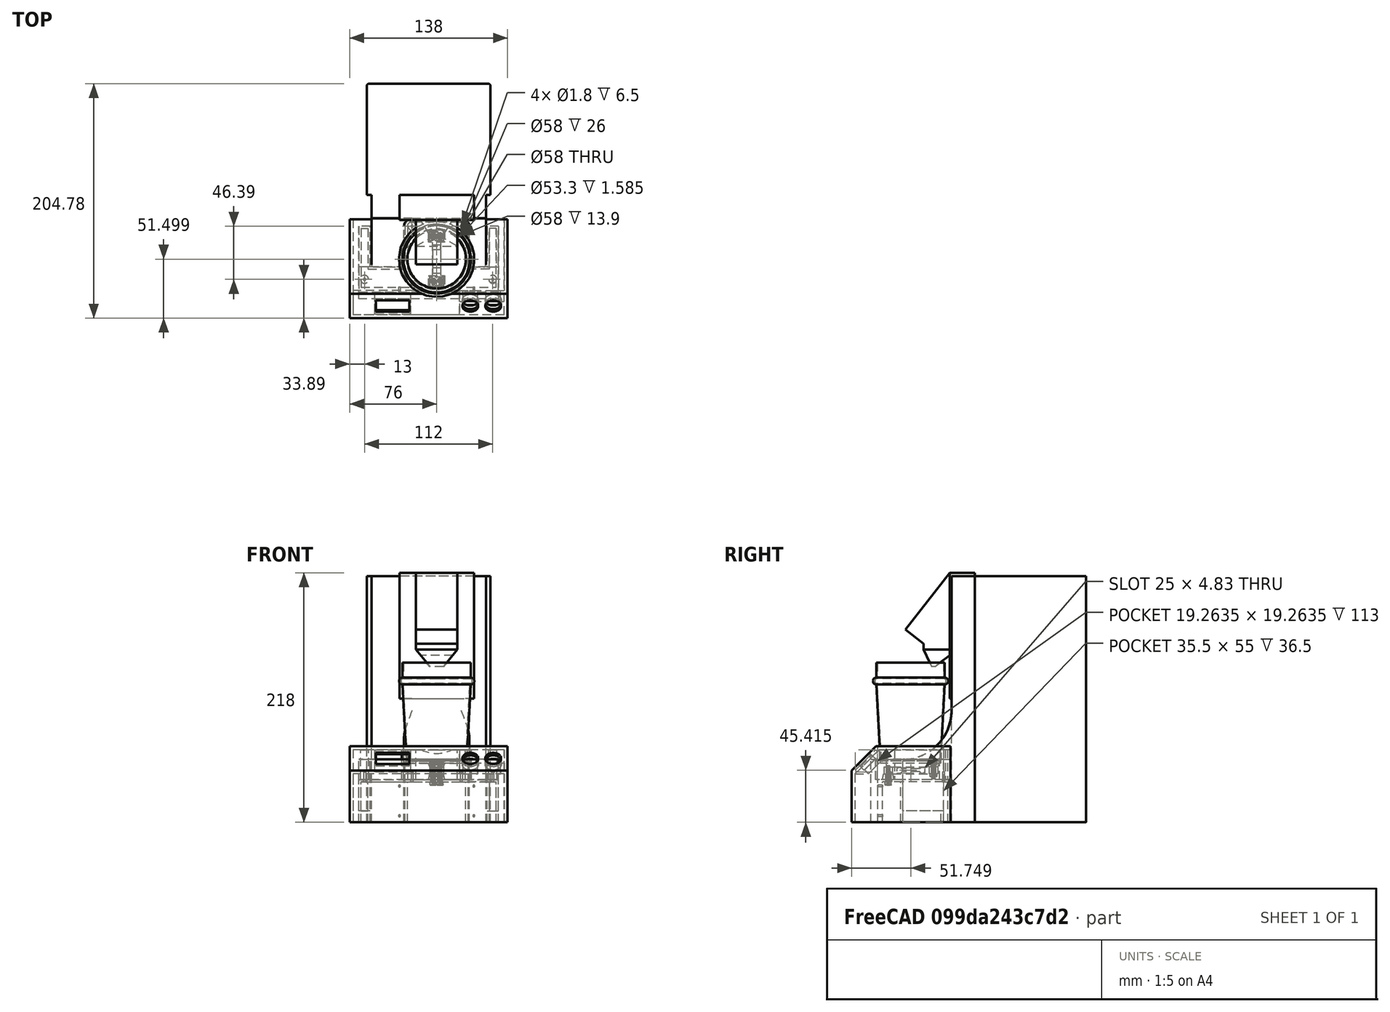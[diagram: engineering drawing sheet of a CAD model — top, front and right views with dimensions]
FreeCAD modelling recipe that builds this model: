
FCSTD DOCUMENT  (FreeCAD 0.20R29410 (Git))
Label: muehle-waage
License: All rights reserved
LicenseURL: http://en.wikipedia.org/wiki/All_rights_reserved
objects: Sketcher::SketchObject×45, PartDesign::Plane×34, PartDesign::Pad×21, PartDesign::Pocket×18, PartDesign::ShapeBinder×14, PartDesign::Body×10, Mesh::Feature×9, Part::FeaturePython×6, Part::Cut×3, PartDesign::AdditiveLoft×2, Spreadsheet::Sheet×1, PartDesign::Revolution×1, PartDesign::Fillet×1
note: 198 computed .brp shape members not serialized (recipe doc carries the construction recipe); baked Part::Feature solids carry a one-line shape summary decoded from their .brp

FEATURE [Spreadsheet::Sheet] Spreadsheet  label="s"
  cells = A1=Sketch fuer Muehle Base; C1=Sketch fuer Adapter; E1=Sketch fuer Dose; G1=Base Plate Waage; I1=Waegezelle; K1=Clips; M1=Cover; O1=Display; Q1=Buttons; A2=(alles in mm); K2=sind zu Threaded Inserts geworden; A3=radius_fuss_aussenseite; B3(radius_fuss_aussenseite)=2; C3=spalt_zur_muehle; D3(spalt_zur_muehle)=1; E3=dose_durchmesser; F3(dose_durchmesser)=58; G3=z_m3_schraube_gewinde; H3(z_m3_schraube_gewinde)=16; I3=y_wz_abstand_loecher; J3(y_wz_abstand_loecher)=40; K3=durchmesser_clips_loch; L3(durchmesser_clips_loch)=2; M3=z_hoehe_ueber_base_plate; N3(z_hoehe_ueber_base_plate)=10; O3=display_breite; P3(display_breite)=29; Q3=button_abstand; R3(button_abstand)=10; A4=radius_fuss_innenseite; B4(radius_fuss_innenseite)=7; C4=x_seitlich_von_muehle; D4(x_seitlich_von_muehle)=10; E4=dose_wandstaerke; F4(dose_wandstaerke)=0.9; G4=z_m3_schraube_kopf; H4(z_m3_schraube_kopf)=3.2; I4=y_wz_gesamt; J4(y_wz_gesamt)=47; K4=durchmesser; L4(durchmesser_loch_threaded_inserts)=1.8; M4=y_abstand_cover_zu_vorderseite_teil; N4(y_abstand_cover_zu_vorderseite_teil)=20; O4=display_hoehe; P4(display_hoehe)=14; Q4=button_kappe_durchmesser; R4(button_kappe_durchmesser)=13.8; A5=radius_rueckseite; B5(radius_rueckseite)=2; C5=y_hauptteil; D5(y_hauptteil)=28; E5=dose_durchmesser_ring; F5(dose_durchmesser_ring)=6; G5=z_pad_hoehe_base_plate; H5(z_pad_hoehe_base_plate)=2; I5=y_wz_kurz; J5(y_wz_kurz)=7.5; K5=pocket_depth_threaded_inserts; L5(pocket_depth_threaded_inserts)=6.5; M5=dicke_cover; N5(dicke_cover)=3; O5=display_pcb_breite; P5(display_pcb_breite)=31; Q5=button_kappe_hoehe; R5(button_kappe_hoehe)=4; E6=dose_durchmesser_unten; F6(dose_durchmesser_unten)=52.8; G6=durchmesser_m3_schraube_kopf; H6(durchmesser_m3_schraube_kopf)=5.5; I6=x_wz_min; J6(x_wz_min)=7; M6=laenge_schraege_seite; N6(laenge_schraege_seite)=30; O6=display_pcb_hoehe; P6(display_pcb_hoehe)=25; Q6=button_kappe_ueberstand; R6(button_kappe_ueberstand)=1; C7=adapter_pad_hoehe; D7(adapter_pad_hoehe)=55; G7=z_standoff_hoehe; H7(z_standoff_hoehe)=3; I7=x_wz_max; J7(x_wz_max)=12; M7=x_ueberstand_cover; N7(x_ueberstand_cover)=5; O7=display_extrusion; P7(display_extrusion)=2; Q7=button_kappe_durchmesser_gross; R7(button_kappe_durchmesser_gross)=14; E8=y_abstand_dose; F8(y_abstand_dose)=-12; G8=y_standoff_gross; H8(y_standoff_gross)=10; I8=x_wz_abstand_loecher; J8(x_wz_abstand_loecher)=6; M8=x_pad_cover; N8(x_pad_cover)==breite_gesamt_unten + 2 * spalt_zur_muehle + 2 * x_seitlich_von_muehle + 2 * x_ueberstand_cover; O8=display_pcb_extrusion; P8(display_pcb_extrusion)=5; Q8=button_kappe_gross_hoehe; R8(button_kappe_gross_hoehe)=4.5; A9=hoehe_gesamt; B9(hoehe_gesamt)=160; C9=spalt_zur_dose; D9(spalt_zur_dose)=0.5; G9=y_standoff_klein; H9(y_standoff_klein)=8; I9=durchmesser_wz_loecher_klein; J9(durchmesser_wz_loecher_klein)=3; M9=dose_verstaerkung_breite; N9(dose_verstaerkung_breite)=1.5; P9=actually 1, but made larger for booleon subtraction from cover; Q9=button_base_seitenlaenge; R9(button_base_seitenlaenge)=13; A10=hoehe_blech; B10(hoehe_blech)=97; E10=z_dose_hoehe; F10(z_dose_hoehe)=86; G10=x_standoff_gross; H10(x_standoff_gross)=14; I10=durchmesser_wz_loecher_gross; J10(durchmesser_wz_loecher_gross)=3.5; M10=dose_verstaerkung_pad; N10(dose_verstaerkung_pad)=5; O10=display_abstand_von_links; P10(display_abstand_von_links)=20; Q10=button_base_extrusion; R10(button_base_extrusion)=15; A11=hoehe_fuss; B11(hoehe_fuss)=42.5; E11=z_abstand_dose_von_schnauze; F11(z_abstand_dose_von_schnauze)=16; G11=x_standoff_klein; H11(x_standoff_klein)=12; I11=z_wz_pad; J11(z_wz_pad)=6; M11=durchmesser_pillars; N11(durchmesser_pillars)=7; O11=ende_display_von_links; P11(ende_display_von_links)==display_abstand_von_links + display_breite; R11=actually 3,5, but cranked up to fit; A12=breite_gesamt_oben; B12(breite_gesamt_oben)=108; C12="Teil" an der WZ; E12=z_dose_oberhalb_ring; F12(z_dose_oberhalb_ring)=13; G12=spalt_pocket_schraubenkopf; H12(spalt_pocket_schraubenkopf)=0.3; I12=durchmesser_wz_bohrung; J12(durchmesser_wz_bohrung)=5; Q12=button1_abstand_von_links; A13=breite_gesamt_unten; B13(breite_gesamt_unten)=100; C13=z_standoff_hoehe_am_teil; D13(z_standoff_hoehe_am_teil)=5; I13=y_laenge_wz_slot; J13(y_laenge_wz_slot)=25; A14=breite_zwischen_fuessen; B14(breite_zwischen_fuessen)=58; C14=y_abstand_standoff_vorderseite; D14(y_abstand_standoff_vorderseite)=4; E14=dose_fillet_radius; F14(dose_fillet_radius)=2; I14=z_hoehe_wz_slot; J14(z_hoehe_wz_slot)=2.5; A15=breite_linker_fuss; B15(breite_linker_fuss)=28.5; C15=wandstaerke_pocket_mitte; D15(wandstaerke_pocket_mitte)=2; A16=breite_rechter_fuss; B16(breite_rechter_fuss)=14.5; C17=m3_bohrung (WZ); D17(m3_bohrung)=4; A18=extrusion_hoehe_muehle; B18(extrusion_hoehe_muehle)=215; C18=m2_bohrung (MoBo); D18(m2_bohrung)=1.8; A19=extrusion_hoehe_fuesse; B19(extrusion_hoehe_fuesse)=55; C19=x_abstand_threaded_inserts; D19(x_abstand_threaded_inserts)=65; C20=z_abstand_threaded_inserts; D20(z_abstand_threaded_inserts)==32 - 3 - 3; A21=x_muehle_verzierung; B21(x_muehle_verzierung)=65; C21=x_abstand_threaded_inserts_von_seite; D21(x_abstand_threaded_inserts_von_seite)=17; A22=y_extrusion_muehle_verzierung; B22(y_extrusion_muehle_verzierung)==hoehe_gesamt - hoehe_blech - hoehe_fuss + y_offset_muehle_verzierung; C22=m3_mutter_breite; D22(m3_mutter_breite)=4; E22=!! actually M2 :/; A23=z_verzierung; B23(z_verzierung)=110; C23=m3_mutter_hoehe; D23(m3_mutter_hoehe)=1.6; E23=!! actually M2 :/; A24=y_offset_muehle_verzierung; B24(y_offset_muehle_verzierung)=1.5; A25=z_offset_muehle_verzierung; +28 more cells
FEATURE [Sketcher::SketchObject] Sketch  label="muehle_base"
  FullyConstrained = true
  MapMode = 5
  Support = -> [XY_Plane]
  expr: Constraints[47] = <<s>>.radius_fuss_aussenseite
  expr: Constraints[48] = <<s>>.radius_fuss_aussenseite
  expr: Constraints[50] = <<s>>.radius_fuss_innenseite
  expr: Constraints[53] = Spreadsheet.breite_gesamt_oben
  expr: Constraints[54] = <<s>>.breite_gesamt_unten
  expr: Constraints[55] = <<s>>.hoehe_gesamt
  expr: Constraints[57] = <<s>>.radius_rueckseite
  expr: Constraints[58] = <<s>>.hoehe_blech
  expr: Constraints[59] = <<s>>.breite_linker_fuss
  expr: Constraints[60] = <<s>>.hoehe_fuss
  expr: Constraints[61] = <<s>>.breite_rechter_fuss
  sketch-geometry (20):
    g0: LineSegment StartX=-54 StartY=95 StartZ=0 EndX=-54 EndY=0 EndZ=0
    g1: LineSegment StartX=-54 StartY=0 StartZ=0 EndX=-50 EndY=0 EndZ=0
    g2: LineSegment StartX=-50 StartY=0 StartZ=0 EndX=-50 EndY=-61 EndZ=0
    g3: ArcOfCircle CenterX=-48 CenterY=-61 CenterZ=0 NormalX=0 NormalY=0 NormalZ=1 AngleXU=0 Radius=2 StartAngle=3.14159 EndAngle=4.71239
    g4: LineSegment StartX=-48 StartY=-63 StartZ=0 EndX=-23.5 EndY=-63 EndZ=0
    g5: ArcOfCircle CenterX=-23.5 CenterY=-61 CenterZ=0 NormalX=0 NormalY=0 NormalZ=1 AngleXU=0 Radius=2 StartAngle=4.71239 EndAngle=6.28319
    g6: LineSegment StartX=-21.5 StartY=-61 StartZ=0 EndX=-21.5 EndY=-27.5 EndZ=0
    g7: ArcOfCircle CenterX=-14.5 CenterY=-27.5 CenterZ=0 NormalX=0 NormalY=0 NormalZ=1 AngleXU=0 Radius=7 StartAngle=1.5708 EndAngle=3.14159
    g8: LineSegment StartX=-14.5 StartY=-20.5 StartZ=0 EndX=28.5 EndY=-20.5 EndZ=0
    g9: ArcOfCircle CenterX=28.5 CenterY=-27.5 CenterZ=0 NormalX=0 NormalY=0 NormalZ=1 AngleXU=0 Radius=7 StartAngle=0 EndAngle=1.5708
    g10: LineSegment StartX=35.5 StartY=-27.5 StartZ=0 EndX=35.5 EndY=-61 EndZ=0
    g11: ArcOfCircle CenterX=37.5 CenterY=-61 CenterZ=0 NormalX=0 NormalY=0 NormalZ=1 AngleXU=0 Radius=2 StartAngle=3.14159 EndAngle=4.71239
    g12: LineSegment StartX=37.5 StartY=-63 StartZ=0 EndX=48 EndY=-63 EndZ=0
    g13: ArcOfCircle CenterX=48 CenterY=-61 CenterZ=0 NormalX=0 NormalY=0 NormalZ=1 AngleXU=0 Radius=2 StartAngle=4.71239 EndAngle=6.28319
    g14: LineSegment StartX=50 StartY=-61 StartZ=0 EndX=50 EndY=0 EndZ=0
    g15: LineSegment StartX=50 StartY=0 StartZ=0 EndX=54 EndY=0 EndZ=0
    g16: LineSegment StartX=54 StartY=0 StartZ=0 EndX=54 EndY=95 EndZ=0
    g17: ArcOfCircle CenterX=52 CenterY=95 CenterZ=0 NormalX=0 NormalY=0 NormalZ=1 AngleXU=0 Radius=2 StartAngle=1.9e-15 EndAngle=1.5708
    g18: LineSegment StartX=52 StartY=97 StartZ=0 EndX=-52 EndY=97 EndZ=0
    g19: ArcOfCircle CenterX=-52 CenterY=95 CenterZ=0 NormalX=0 NormalY=0 NormalZ=1 AngleXU=0 Radius=2 StartAngle=1.5708 EndAngle=3.14159
  constraints (62):
    c: Vertical(g0)
    c: Horizontal(g1)
    c: Coincident(g1,g2)
    c: Tangent(g2,g3) = -1.5708
    c: Coincident(g3,g4)
    c: Horizontal(g4)
    c: Tangent(g4,g5) = -1.5708
    c: Coincident(g5,g6)
    c: Vertical(g6)
    c: Tangent(g6,g7) = 1.5708
    c: Coincident(g7,g8)
    c: Horizontal(g8)
    c: Tangent(g8,g9) = 1.5708
    c: Coincident(g9,g10)
    c: Vertical(g10)
    c: Tangent(g10,g11) = -1.5708
    c: Coincident(g11,g12)
    c: Horizontal(g12)
    c: Coincident(g13,g14)
    c: Vertical(g14)
    c: Coincident(g14,g15)
    c: Coincident(g15,g16)
    c: Vertical(g16)
    c: Tangent(g16,g17) = -1.5708
    c: Coincident(g17,g18)
    c: Horizontal(g18)
    c: Coincident(g19,g0)
    c: Horizontal(g0,g16)
    c: Coincident(g1,g0)
    c: Horizontal(g15)
    c: Horizontal(g2,g5)
    c: Horizontal(g10,g13)
    c: Horizontal(g6,g9)
    c: Coincident(g19,g18)
    c: Vertical(g18,g19)
    c: Symmetric(g0,g15,g-1)
    c: Vertical(g11,g11)
    c: Coincident(g12,g13)
    c: Horizontal(g13,g13)
    c: Vertical(g13,g12)
    c: Horizontal(g9,g9)
    c: Vertical(g7,g7)
    c: Horizontal(g2,g3)
    c: Horizontal(g3,g3)
    c: Horizontal(g3,g5)
    c: Horizontal(g5,g5)
    c: Vertical(g3,g3)
    c: Radius(g3) = 2
    c: Radius(g11) = 2
    c: Horizontal(g10,g5)
    c: Radius(g7) = 7
    c: Vertical(g17,g17)
    c: Symmetric(g1,g14,g-2)
    c: DistanceX(g0,g16) = 108
    c: DistanceX(g2,g13) = 100
    c: DistanceY(g3,g18) = 160
    c: Horizontal(g19,g0)
    c: Radius(g19) = 2
    c: DistanceY(g0,g18) = 97
    c: DistanceX(g2,g5) = 28.5
    c: DistanceY(g4,g7) = 42.5
    c: DistanceX(g10,g13) = 14.5
FEATURE [PartDesign::Pad] Pad
  Direction = (0,0,1)
  Length = 215
  Length2 = 10
  Profile = -> Sketch
  ReferenceAxis = -> Sketch [N_Axis]
  Type = 0
  expr: Length = <<s>>.extrusion_hoehe_muehle
FEATURE [PartDesign::Plane] DatumPlane  label="DatumPlanePocketFuss"
  Length = 199.436
  MapMode = 5
  Placement = pos=(50,0,0) rot=(0.57735,0.57735,0.57735;2.0944rad)
  ResizeMode = 0
  Support = -> [Pad]
  Width = 282.436
FEATURE [Sketcher::SketchObject] Sketch001
  ExternalGeometry = -> [Pad]
  FullyConstrained = true
  MapMode = 5
  Placement = pos=(50,0,0) rot=(0.57735,0.57735,0.57735;2.0944rad)
  Support = -> [DatumPlane]
  expr: Constraints[10] = <<s>>.hoehe_fuss
  expr: Constraints[13] = <<s>>.extrusion_hoehe_fuesse
  sketch-geometry (5):
    g0: LineSegment StartX=-20.5 StartY=220 StartZ=0 EndX=-20.5 EndY=97.5 EndZ=0
    g1: ArcOfCircle CenterX=-63 CenterY=97.5 CenterZ=0 NormalX=0 NormalY=0 NormalZ=1 AngleXU=0 Radius=42.5 StartAngle=4.71239 EndAngle=6.28319
    g2: LineSegment StartX=-63 StartY=55 StartZ=0 EndX=-68 EndY=55 EndZ=0
    g3: LineSegment StartX=-68 StartY=55 StartZ=0 EndX=-68 EndY=220 EndZ=0
    g4: LineSegment StartX=-68 StartY=220 StartZ=0 EndX=-20.5 EndY=220 EndZ=0
  constraints (14):
    c: Vertical(g0)
    c: Tangent(g0,g1) = 1.5708
    c: Tangent(g1,g2) = 1.5708
    c: Coincident(g2,g3)
    c: Vertical(g3)
    c: Coincident(g3,g4)
    c: Coincident(g4,g0)
    c: Horizontal(g4)
    c: PointOnObject(g1,g-3)
    c: Vertical(g1,g1)
    c: Radius(g1) = 42.5
    c: DistanceY(g-3,g3) = 5
    c: DistanceX(g3,g-3) = 5
    c: DistanceY(g-3,g1) = 55
FEATURE [PartDesign::Pocket] Pocket
  BaseFeature = -> Pad
  Direction = (-1,0,0)
  Length = 5
  Length2 = 5
  Profile = -> Sketch001
  ReferenceAxis = -> Sketch001 [N_Axis]
  Type = 1
FEATURE [PartDesign::Plane] DatumPlane001  label="DatumPlaneVerzierungMuehle"
  Length = 140.4
  MapMode = 5
  Placement = pos=(0,0,0) rot=(1,0,0;1.5708rad)
  ResizeMode = 0
  Support = -> [Pocket]
  Width = 275.4
FEATURE [Mesh::Feature] Mesh  label="TestMesh001"
FEATURE [PartDesign::Plane] DatumPlane004  label="DatumPlaneMitteVonSchnauze"
  AttachmentOffset = pos=(0,0,7) rot=(0,0,1;0rad)
  Length = 199.436
  MapMode = 5
  Placement = pos=(7,-1.6e-15,1.6e-15) rot=(0.57735,0.57735,0.57735;2.0944rad)
  ResizeMode = 0
  Support = -> [YZ_Plane]
  Width = 282.436
  expr: .AttachmentOffset.Base.z = <<s>>.offset_yz
FEATURE [Sketcher::SketchObject] Sketch003  label="SketchVerzierung"
  ExternalGeometry = -> [Pocket,DatumPlane004]
  FullyConstrained = true
  MapMode = 5
  Placement = pos=(0,0,0) rot=(1,0,0;1.5708rad)
  Support = -> [DatumPlane001]
  expr: Constraints[7] = Spreadsheet.x_muehle_verzierung
  expr: Constraints[8] = Spreadsheet.z_verzierung
  expr: Constraints[9] = <<s>>.z_offset_muehle_verzierung
  sketch-geometry (4):
    g0: LineSegment StartX=-25.5 StartY=218 StartZ=0 EndX=-25.5 EndY=108 EndZ=0
    g1: LineSegment StartX=-25.5 StartY=108 StartZ=0 EndX=39.5 EndY=108 EndZ=0
    g2: LineSegment StartX=39.5 StartY=108 StartZ=0 EndX=39.5 EndY=218 EndZ=0
    g3: LineSegment StartX=39.5 StartY=218 StartZ=0 EndX=-25.5 EndY=218 EndZ=0
  constraints (11):
    c: Coincident(g0,g1)
    c: Coincident(g1,g2)
    c: Coincident(g2,g3)
    c: Coincident(g3,g0)
    c: Horizontal(g3)
    c: Vertical(g0)
    c: Vertical(g2)
    c: DistanceX(g3,g3) = 65
    c: DistanceY(g0,g0) = 110
    c: DistanceY(g-3,g0) = 3
    c: Symmetric(g0,g1,g-4)
FEATURE [PartDesign::Pad] Pad002  label="PadVerzierung"
  BaseFeature = -> Pocket
  Direction = (0,-1,2e-16)
  Length = 22
  Length2 = 10
  Profile = -> Sketch003
  ReferenceAxis = -> Sketch003 [N_Axis]
  Type = 0
  expr: Length = <<s>>.y_extrusion_muehle_verzierung
FEATURE [Sketcher::SketchObject] Sketch004  label="SketchSchnauze"
  ExternalGeometry = -> [Pad002]
  FullyConstrained = true
  MapMode = 2
  Placement = pos=(7,-1.6e-15,1.6e-15) rot=(0.57735,0.57735,0.57735;2.0944rad)
  Support = -> [DatumPlane004]
  expr: Constraints[7] = <<s>>.z_schnauze
  expr: Constraints[8] = <<s>>.y_schnauze
  expr: Constraints[9] = <<s>>.l_schnauze_schraege
  sketch-geometry (4):
    g0: LineSegment StartX=-22 StartY=218 StartZ=0 EndX=-60.7693 EndY=168.302 EndZ=0
    g1: LineSegment StartX=-60.7693 StartY=168.302 StartZ=0 EndX=-45 EndY=156 EndZ=0
    g2: LineSegment StartX=-45 StartY=156 StartZ=0 EndX=-22 EndY=156 EndZ=0
    g3: LineSegment StartX=-22 StartY=156 StartZ=0 EndX=-22 EndY=218 EndZ=0
  constraints (11):
    c: Coincident(g0,g1)
    c: Coincident(g1,g2)
    c: Horizontal(g2)
    c: Coincident(g2,g3)
    c: Coincident(g3,g0)
    c: Vertical(g3)
    c: Coincident(g0,g-3)
    c: DistanceY(g3,g3) = 62
    c: DistanceX(g2,g2) = 23
    c: Distance(g1) = 20
    c: Angle(g1,g0) = 1.5708
FEATURE [PartDesign::Pad] Pad003  label="PadSchnauze"
  BaseFeature = -> Pad002
  Direction = (1,-1e-16,1e-16)
  Length = 36
  Length2 = 10
  Midplane = true
  Profile = -> Sketch004
  ReferenceAxis = -> Sketch004 [N_Axis]
  Type = 0
  expr: Length = <<s>>.x_schnauze
FEATURE [PartDesign::Plane] DatumPlane002  label="DatumPlanePlastikPadUnterSchnauze"
  Length = 140.4
  MapMode = 5
  Placement = pos=(0,-22,4.9e-15) rot=(1,0,0;1.5708rad)
  ResizeMode = 0
  Support = -> [Pad003]
  Width = 275.4
FEATURE [Sketcher::SketchObject] Sketch005  label="SketchPlastikUnterSchnauze"
  ExternalGeometry = -> [Pad003,DatumPlane004]
  FullyConstrained = true
  MapMode = 5
  Placement = pos=(0,-22,4.9e-15) rot=(1,0,0;1.5708rad)
  Support = -> [DatumPlane002]
  expr: Constraints[0] = <<s>>.x_kurz_plastik_unter_schnauze
  expr: Constraints[1] = <<s>>.z_plastik_unter_schnauze
  expr: Constraints[9] = <<s>>.z_lippe_plastik_unter_schnauze
  sketch-geometry (6):
    g0: LineSegment StartX=13 StartY=136 StartZ=0 EndX=1 EndY=136 EndZ=0
    g1: LineSegment StartX=-11 StartY=156 StartZ=0 EndX=-11 EndY=151 EndZ=0
    g2: LineSegment StartX=-11 StartY=151 StartZ=0 EndX=1 EndY=136 EndZ=0
    g3: LineSegment StartX=25 StartY=156 StartZ=0 EndX=25 EndY=151 EndZ=0
    g4: LineSegment StartX=25 StartY=151 StartZ=0 EndX=13 EndY=136 EndZ=0
    g5: LineSegment StartX=-11 StartY=156 StartZ=0 EndX=25 EndY=156 EndZ=0
  constraints (15):
    c: DistanceX(g0,g0) = 12
    c: DistanceY(g0,g-3) = 20
    c: Vertical(g1)
    c: Coincident(g1,g2)
    c: Coincident(g2,g0)
    c: Coincident(g3,g4)
    c: Coincident(g4,g0)
    c: Vertical(g3)
    c: Horizontal(g3,g1)
    c: DistanceY(g1,g1) = 5
    c: Symmetric(g0,g0,g-4)
    c: Coincident(g1,g-3)
    c: Symmetric(g3,g1,g-4)
    c: Coincident(g5,g1)
    c: Coincident(g5,g3)
FEATURE [PartDesign::Pad] Pad004  label="PadMuehleKomplett"
  BaseFeature = -> Pad003
  Direction = (0,-1,2e-16)
  Length = 23
  Length2 = 10
  Profile = -> Sketch005
  ReferenceAxis = -> Sketch005 [N_Axis]
  Type = 0
  expr: Length = <<s>>.y_extrusion_plastik_unter_schnauze
FEATURE [PartDesign::Plane] DatumPlane003  label="DatumPlanePlastikUnterSchnauzePocket"
  Length = 199.436
  MapMode = 5
  Placement = pos=(25,0,0) rot=(0.57735,0.57735,0.57735;2.0944rad)
  ResizeMode = 0
  Support = -> [Pad004]
  Width = 282.436
FEATURE [Sketcher::SketchObject] Sketch007
  ExternalGeometry = -> [Pad004]
  FullyConstrained = true
  MapMode = 5
  Placement = pos=(25,0,0) rot=(0.57735,0.57735,0.57735;2.0944rad)
  Support = -> [DatumPlane003]
  expr: Constraints[14] = <<s>>.y_plastik_unter_schnauze_pocket_kurz
  expr: Constraints[17] = <<s>>.y_abstand_plastik_unter_schnauze_von_muehle_body_unten
  expr: Constraints[19] = <<s>>.z_plastik_unter_schnauze_pocket_hinten
  sketch-geometry (7):
    g0: LineSegment StartX=-45 StartY=151 StartZ=0 EndX=-38 EndY=136 EndZ=0
    g1: LineSegment StartX=-38 StartY=136 StartZ=0 EndX=-35 EndY=136 EndZ=0
    g2: LineSegment StartX=-35 StartY=136 StartZ=0 EndX=-22 EndY=146 EndZ=0
    g3: LineSegment StartX=-45 StartY=151 StartZ=0 EndX=-46 EndY=151 EndZ=0
    g4: LineSegment StartX=-46 StartY=151 StartZ=0 EndX=-46 EndY=135 EndZ=0
    g5: LineSegment StartX=-46 StartY=135 StartZ=0 EndX=-22 EndY=135 EndZ=0
    g6: LineSegment StartX=-22 StartY=135 StartZ=0 EndX=-22 EndY=146 EndZ=0
  constraints (20):
    c: Coincident(g-3,g0)
    c: Coincident(g0,g1)
    c: Horizontal(g1)
    c: Coincident(g1,g2)
    c: Coincident(g0,g3)
    c: Horizontal(g3)
    c: Coincident(g3,g4)
    c: Vertical(g4)
    c: Coincident(g4,g5)
    c: Horizontal(g5)
    c: Coincident(g5,g6)
    c: Coincident(g6,g2)
    c: Vertical(g6)
    c: Horizontal(g0,g-4)
    c: DistanceX(g1,g1) = 3
    c: DistanceX(g4,g-4) = 1
    c: DistanceY(g4,g-4) = 1
    c: DistanceX(g0,g-5) = 16
    c: Vertical(g-5,g2)
    c: DistanceY(g2,g-3) = 10
FEATURE [PartDesign::Pocket] Pocket001  label="PocketPlastikUnterSchnauze"
  AlongSketchNormal = false
  BaseFeature = -> Pad004
  Direction = (-1,0,0)
  Length = 5
  Length2 = 5
  Profile = -> Sketch007
  ReferenceAxis = -> Sketch007 [N_Axis]
  Type = 1
FEATURE [PartDesign::Body] Body  label="muehle"
  Group = -> [Sketch,Pad,DatumPlane,Sketch001,Pocket,DatumPlane004,DatumPlane001,Sketch003,Pad002,Sketch004,Pad003,DatumPlane002,Sketch005,Pad004,DatumPlane003,Sketch007,Pocket001]
  Origin = -> Origin
  Tip = -> Pocket001
FEATURE [PartDesign::ShapeBinder] ShapeBinder002  label="ShapeBinderMuehle001"
  Support = -> [Sketch]
  TraceSupport = false
FEATURE [Sketcher::SketchObject] Sketch002  label="sketch_adapter"
  ExternalGeometry = -> [ShapeBinder002]
  FullyConstrained = true
  MapMode = 5
  Support = -> [XY_Plane003]
  expr: Constraints[24] = Spreadsheet.x_seitlich_von_muehle
  expr: Constraints[25] = Spreadsheet.y_hauptteil
  expr: Constraints[38] = <<s>>.spalt_zur_muehle
  expr: Constraints[41] = <<s>>.spalt_zur_muehle
  expr: Constraints[42] = <<s>>.spalt_zur_muehle
  sketch-geometry (14):
    g0: LineSegment StartX=-61 StartY=-27.5 StartZ=0 EndX=-51 EndY=-27.5 EndZ=0
    g1: LineSegment StartX=-51 StartY=-27.5 StartZ=0 EndX=-51 EndY=-63 EndZ=0
    g2: LineSegment StartX=-51 StartY=-63 StartZ=0 EndX=-20.5 EndY=-63 EndZ=0
    g3: LineSegment StartX=-20.5 StartY=-63 StartZ=0 EndX=-20.5 EndY=-27.5 EndZ=0
    g4: LineSegment StartX=34.5 StartY=-27.5 StartZ=0 EndX=34.5 EndY=-63 EndZ=0
    g5: LineSegment StartX=34.5 StartY=-63 StartZ=0 EndX=51 EndY=-63 EndZ=0
    g6: LineSegment StartX=51 StartY=-63 StartZ=0 EndX=51 EndY=-27.5 EndZ=0
    g7: LineSegment StartX=51 StartY=-27.5 StartZ=0 EndX=61 EndY=-27.5 EndZ=0
    g8: LineSegment StartX=61 StartY=-27.5 StartZ=0 EndX=61 EndY=-91 EndZ=0
    g9: LineSegment StartX=61 StartY=-91 StartZ=0 EndX=-61 EndY=-91 EndZ=0
    g10: LineSegment StartX=-61 StartY=-91 StartZ=0 EndX=-61 EndY=-27.5 EndZ=0
    g11: LineSegment StartX=-14.5 StartY=-21.5 StartZ=0 EndX=28.5 EndY=-21.5 EndZ=0
    g12: ArcOfCircle CenterX=-14.5 CenterY=-27.5 CenterZ=0 NormalX=0 NormalY=0 NormalZ=1 AngleXU=0 Radius=6 StartAngle=1.5708 EndAngle=3.14159
    g13: ArcOfCircle CenterX=28.5 CenterY=-27.5 CenterZ=0 NormalX=0 NormalY=0 NormalZ=1 AngleXU=0 Radius=6 StartAngle=0 EndAngle=1.5708
  constraints (43):
    c: Horizontal(g0)
    c: Coincident(g0,g1)
    c: Vertical(g1)
    c: Coincident(g1,g2)
    c: Horizontal(g2)
    c: Coincident(g2,g3)
    c: Vertical(g3)
    c: Vertical(g4)
    c: Coincident(g4,g5)
    c: Horizontal(g5)
    c: Coincident(g5,g6)
    c: Vertical(g6)
    c: Coincident(g6,g7)
    c: Horizontal(g7)
    c: Coincident(g7,g8)
    c: Vertical(g8)
    c: Coincident(g8,g9)
    c: Horizontal(g9)
    c: Coincident(g9,g10)
    c: Coincident(g10,g0)
    c: Vertical(g10)
    c: Horizontal(g0,g3)
    c: Horizontal(g4,g6)
    c: Equal(g0,g7)
    c: DistanceX(g0,g0) = 10
    c: DistanceY(g9,g1) = 28
    c: Horizontal(g4,g2)
    c: Horizontal(g11)
    c: Coincident(g12,g3)
    c: Coincident(g12,g11)
    c: Horizontal(g3,g12)
    c: Vertical(g12,g11)
    c: Horizontal(g12,g4)
    c: Coincident(g13,g11)
    c: Coincident(g13,g4)
    c: Horizontal(g13,g4)
    c: Vertical(g11,g13)
    c: Coincident(g-10,g12)
    c: DistanceY(g11,g-10) = 1
    c: Vertical(g-9,g11)
    c: Horizontal(g2,g-7)
    c: DistanceX(g1,g-3) = 1
    c: DistanceX(g-4,g5) = 1
FEATURE [PartDesign::Pad] Pad005
  Direction = (0,0,1)
  Length = 55
  Length2 = 10
  Profile = -> Sketch002
  ReferenceAxis = -> Sketch002 [N_Axis]
  Type = 0
  expr: Length = <<s>>.adapter_pad_hoehe
FEATURE [Mesh::Feature] Mesh001  label="TestMesh002"
FEATURE [Mesh::Feature] Mesh002  label="PocketSchraubenKopf (Meshed)"
FEATURE [Part::FeaturePython] Screw001  label="M3x12-Screw"  # Fasteners workbench fastener (typed FeaturePython)
  Placement = pos=(10,-36.2806,50.2148) rot=(0,0,1;0rad)
  baseObject = -> Body004 [Edge22]
  diameter = 4
  invert = false
  leftHanded = false
  length = 4
  lengthCustom = 12
  matchOuter = true
  offset = 0
  thread = true
  type = 48
FEATURE [Part::FeaturePython] Screw  label="M3x12-Screw001"  # Fasteners workbench fastener (typed FeaturePython)
  Placement = pos=(4,-36.2806,50.2148) rot=(0,0,1;0rad)
  baseObject = -> Body004 [Edge23]
  diameter = 4
  invert = false
  leftHanded = false
  length = 4
  lengthCustom = 12
  matchOuter = true
  offset = 0
  thread = true
  type = 48
FEATURE [Part::FeaturePython] Nut  label="M3-Nut"  # Fasteners workbench fastener (typed FeaturePython)
  Placement = pos=(10,-36.2806,42.4148) rot=(0.727357,0.68626,0;3.14159rad)
  baseObject = -> Body005 [Edge34]
  diameter = 4
  invert = true
  leftHanded = false
  matchOuter = true
  offset = 0
  thread = false
  type = 25
FEATURE [Part::FeaturePython] Nut001  label="M3-Nut001"  # Fasteners workbench fastener (typed FeaturePython)
  Placement = pos=(4,-36.2806,42.4148) rot=(0.727357,0.68626,0;3.14159rad)
  baseObject = -> Body005 [Edge36]
  diameter = 4
  invert = true
  leftHanded = false
  matchOuter = true
  offset = 0
  thread = false
  type = 25
FEATURE [PartDesign::ShapeBinder] ShapeBinder008  label="ShapeBinderSketchAdapter"
  Support = -> [Sketch002]
  TraceSupport = false
FEATURE [Mesh::Feature] Mesh003  label="TeilMitCutsFuerMutterMesh001"
FEATURE [PartDesign::ShapeBinder] ShapeBinder001  label="ShapeBinderMuehleNeu"
  Support = -> [Pocket001]
  TraceSupport = false
FEATURE [Sketcher::SketchObject] Sketch006  label="SketchDose"
  ExternalGeometry = -> [ShapeBinder001]
  FullyConstrained = true
  MapMode = 5
  Placement = pos=(7,-1.6e-15,1.6e-15) rot=(0.57735,0.57735,0.57735;2.0944rad)
  Support = -> [DatumPlane004]
  expr: Constraints[19] = <<s>>.dose_wandstaerke
  expr: Constraints[20] = <<s>>.dose_wandstaerke
  expr: Constraints[23] = <<s>>.dose_wandstaerke
  expr: Constraints[36] = <<s>>.dose_wandstaerke
  expr: Constraints[37] = <<s>>.z_dose_oberhalb_ring
  expr: Constraints[38] = <<s>>.z_dose_hoehe
  expr: Constraints[40] = <<s>>.dose_durchmesser / 2
  expr: Constraints[5] = <<s>>.dose_durchmesser_ring
  expr: Constraints[6] = <<s>>.dose_durchmesser_unten / 2
  sketch-geometry (15):
    g0: ArcOfCircle CenterX=-26.3806 CenterY=123.415 CenterZ=0 NormalX=0 NormalY=0 NormalZ=1 AngleXU=0 Radius=3 StartAngle=4.71239 EndAngle=7.85398
    g1: LineSegment StartX=-26.3806 StartY=120.415 StartZ=0 EndX=-29.8806 EndY=53.4148 EndZ=0
    g2: LineSegment StartX=-29.8806 StartY=53.4148 StartZ=0 EndX=-56.2806 EndY=53.4148 EndZ=0
    g3: LineSegment StartX=-56.2806 StartY=53.4148 StartZ=0 EndX=-56.2806 EndY=139.415 EndZ=0
    g4: LineSegment StartX=-26.3806 StartY=139.415 StartZ=0 EndX=-27.2806 EndY=139.415 EndZ=0
    g5: LineSegment StartX=-27.2806 StartY=139.415 StartZ=0 EndX=-27.2806 EndY=125.515 EndZ=0
    g6: ArcOfCircle CenterX=-27.2806 CenterY=123.415 CenterZ=0 NormalX=0 NormalY=0 NormalZ=1 AngleXU=0 Radius=2.1 StartAngle=4.71239 EndAngle=7.85398
    g7: LineSegment StartX=-27.2806 StartY=121.315 StartZ=0 EndX=-30.7806 EndY=54.3148 EndZ=0
    g8: LineSegment StartX=-30.7806 StartY=54.3148 StartZ=0 EndX=-56.2806 EndY=54.3148 EndZ=0
    g9: LineSegment StartX=-56.2806 StartY=54.3148 StartZ=0 EndX=-56.2806 EndY=53.4148 EndZ=0
    g10: Circle CenterX=-22 CenterY=146 CenterZ=0 NormalX=0 NormalY=0 NormalZ=1 AngleXU=0 Radius=10
    g11: Circle CenterX=-35 CenterY=136 CenterZ=0 NormalX=0 NormalY=0 NormalZ=1 AngleXU=0 Radius=10
    g12: LineSegment StartX=-31.9892 StartY=145.536 StartZ=0 EndX=-25.0108 EndY=136.464 EndZ=0
    g13: LineSegment StartX=-26.3806 StartY=126.415 StartZ=0 EndX=-26.3806 EndY=139.415 EndZ=0
    g14: GeomPoint X=-28.5 Y=141 Z=0
  constraints (44):
    c: Coincident(g0,g1)
    c: Coincident(g1,g2)
    c: Horizontal(g2)
    c: Vertical(g0,g0)
    c: Vertical(g0,g0)
    c: Diameter(g0) = 6
    c: DistanceX(g2,g2) = 26.4
    c: Coincident(g3,g2)
    c: Vertical(g3)
    c: Horizontal(g4)
    c: Coincident(g4,g5)
    c: Vertical(g5)
    c: Perpendicular(g5,g6) = 4.71239
    c: Coincident(g6,g7)
    c: Coincident(g7,g8)
    c: Horizontal(g8)
    c: Coincident(g8,g9)
    c: Vertical(g9)
    c: Coincident(g9,g2)
    c: DistanceX(g7,g1) = 0.9
    c: DistanceY(g1,g7) = 0.9
    c: Vertical(g6,g6)
    c: Horizontal(g6,g0)
    c: DistanceY(g5,g0) = 0.9
    c: Equal(g10,g11)
    c: Diameter(g10) = 20
    c: PointOnObject(g12,g10)
    c: PointOnObject(g12,g10)
    c: PointOnObject(g12,g11)
    c: PointOnObject(g12,g11)
    c: Coincident(g11,g-4)
    c: Coincident(g10,g-4)
    c: PointOnObject(g4,g12)
    c: Coincident(g13,g0)
    c: Coincident(g13,g4)
    c: Vertical(g13)
    c: DistanceX(g5,g0) = 0.9
    c: DistanceY(g0,g4) = 13
    c: DistanceY(g1,g4) = 86
    c: Horizontal(g4,g3)
    c: DistanceX(g3,g4) = 29
    c: PointOnObject(g14,g12)
    c: PointOnObject(g14,g-4)
    c: Distance(g4,g14) = 2
FEATURE [PartDesign::Revolution] Revolution
  Angle = 360
  Axis = (-9.5e-15,9.5e-15,86)
  Base = (7,-56.2806,53.4148)
  Placement = pos=(7,-1.6e-15,1.6e-15) rot=(0.57735,0.57735,0.57735;2.0944rad)
  Profile = -> Sketch006
  ReferenceAxis = -> Sketch006 [Axis0]
  Reversed = true
FEATURE [PartDesign::Fillet] Fillet
  Base = -> Revolution [Edge4]
  Placement = pos=(7,-2e-15,2e-15) rot=(0.57735,0.57735,0.57735;2.0944rad)
  Radius = 2
  SupportTransform = false
  UseAllEdges = false
  expr: Radius = <<s>>.dose_fillet_radius
FEATURE [PartDesign::Body] Body002  label="dose"
  Group = -> [ShapeBinder001,Sketch006,Revolution,Fillet]
  Origin = -> Origin002
  Tip = -> Fillet
FEATURE [PartDesign::ShapeBinder] ShapeBinder003  label="ShapeBinderDoseSketch"
  Placement = pos=(7,-1.6e-15,1.6e-15) rot=(0.57735,0.57735,0.57735;2.0944rad)
  Support = -> [Sketch006]
  TraceSupport = false
FEATURE [PartDesign::ShapeBinder] ShapeBinder004  label="ShapeBinderDoseFillet"
  Placement = pos=(7,-2e-15,2e-15) rot=(0.57735,0.57735,0.57735;2.0944rad)
  Support = -> [Fillet]
  TraceSupport = false
FEATURE [PartDesign::Plane] DatumPlane005  label="DatumPlaneUnterseiteDose"
  Length = 60
  MapMode = 5
  Placement = pos=(7,-1.98e-14,53.4148) rot=(0.707107,0.707107,0;3.14159rad)
  ResizeMode = 0
  Support = -> [ShapeBinder004]
  Width = 60
FEATURE [Sketcher::SketchObject] Sketch008  label="SketchAusschnittDose"
  ExternalGeometry = -> [ShapeBinder003]
  FullyConstrained = true
  MapMode = 5
  Placement = pos=(7,-1.98e-14,53.4148) rot=(0.707107,0.707107,0;3.14159rad)
  Support = -> [DatumPlane005]
  expr: Constraints[1] = <<s>>.dose_durchmesser_unten + <<s>>.spalt_zur_dose
  sketch-geometry (1):
    g0: Circle CenterX=-56.2806 CenterY=0 CenterZ=0 NormalX=0 NormalY=0 NormalZ=1 AngleXU=0 Radius=26.65
  constraints (2):
    c: Coincident(g0,g-3)
    c: Diameter(g0) = 53.3
FEATURE [PartDesign::Pocket] Pocket002
  BaseFeature = -> Pad005
  Direction = (1e-16,-3e-16,1)
  Length = 5
  Length2 = 5
  Profile = -> Sketch008
  ReferenceAxis = -> Sketch008 [N_Axis]
  Type = 1
FEATURE [PartDesign::Body] Body003  label="teil2"
  Group = -> [ShapeBinder002,Sketch002,Pad005,ShapeBinder003,ShapeBinder004,DatumPlane005,Sketch008,Pocket002]
  Origin = -> Origin003
  Tip = -> Pocket002
FEATURE [PartDesign::ShapeBinder] ShapeBinder005  label="ShapeBinderDose"
  Placement = pos=(7,-2e-15,2e-15) rot=(0.57735,0.57735,0.57735;2.0944rad)
  Support = -> [Fillet]
  TraceSupport = false
FEATURE [PartDesign::Plane] DatumPlane006  label="DatumPlaneBasePlateWaage"
  Length = 60
  MapMode = 5
  Placement = pos=(7,-1.98e-14,53.4148) rot=(0.707107,0.707107,0;3.14159rad)
  ResizeMode = 0
  Support = -> [ShapeBinder005]
  Width = 60
FEATURE [Sketcher::SketchObject] Sketch009  label="SketchKreisBasePlate"
  ExternalGeometry = -> [ShapeBinder005]
  FullyConstrained = true
  MapMode = 5
  Placement = pos=(7,-1.98e-14,53.4148) rot=(0.707107,0.707107,0;3.14159rad)
  Support = -> [DatumPlane006]
  expr: Constraints[1] = <<s>>.dose_durchmesser_unten
  sketch-geometry (1):
    g0: Circle CenterX=-56.2806 CenterY=3.29e-14 CenterZ=0 NormalX=0 NormalY=0 NormalZ=1 AngleXU=0 Radius=26.4
  constraints (2):
    c: Coincident(g0,g-3)
    c: Diameter(g0) = 52.8
FEATURE [PartDesign::Pad] Pad006  label="PadKreis"
  Direction = (-1e-16,3e-16,-1)
  Length = 2
  Length2 = 10
  Placement = pos=(7,-1.98e-14,53.4148) rot=(0.707107,0.707107,0;3.14159rad)
  Profile = -> Sketch009
  ReferenceAxis = -> Sketch009 [N_Axis]
  Type = 0
  expr: Length = <<s>>.z_pad_hoehe_base_plate
FEATURE [PartDesign::Plane] DatumPlane007  label="DatumPlaneStandoffTop"
  Length = 60
  MapMode = 5
  Placement = pos=(7,-1.83e-14,51.4148) rot=(0.707107,0.707107,0;3.14159rad)
  ResizeMode = 0
  Support = -> [Pad006]
  Width = 60
FEATURE [PartDesign::Plane] DatumPlane008  label="DatumPlaneStandoffBottom"
  AttachmentOffset = pos=(0,0,3) rot=(0,0,1;0rad)
  Length = 62.7499
  MapMode = 11
  Placement = pos=(7,-56.2806,48.4148) rot=(1,0,0;3.14159rad)
  ResizeMode = 0
  Support = -> [Pad006]
  Width = 94.0305
  expr: .AttachmentOffset.Base.z = <<s>>.z_standoff_hoehe
FEATURE [Sketcher::SketchObject] Sketch010  label="SketchStandoffTop"
  ExternalGeometry = -> [Pad006]
  FullyConstrained = true
  MapMode = 5
  Placement = pos=(7,-1.83e-14,51.4148) rot=(0.707107,0.707107,0;3.14159rad)
  Support = -> [DatumPlane007]
  expr: Constraints[10] = <<s>>.y_wz_abstand_loecher / 2
  expr: Constraints[11] = <<s>>.y_standoff_gross
  expr: Constraints[12] = <<s>>.x_standoff_gross
  sketch-geometry (5):
    g0: LineSegment StartX=-41.2806 StartY=7 StartZ=0 EndX=-41.2806 EndY=-7 EndZ=0
    g1: LineSegment StartX=-41.2806 StartY=-7 StartZ=0 EndX=-31.2806 EndY=-7 EndZ=0
    g2: LineSegment StartX=-31.2806 StartY=-7 StartZ=0 EndX=-31.2806 EndY=7 EndZ=0
    g3: LineSegment StartX=-31.2806 StartY=7 StartZ=0 EndX=-41.2806 EndY=7 EndZ=0
    g4: GeomPoint X=-36.2806 Y=0 Z=0
  constraints (13):
    c: Coincident(g0,g1)
    c: Coincident(g1,g2)
    c: Coincident(g2,g3)
    c: Coincident(g3,g0)
    c: Horizontal(g1)
    c: Horizontal(g3)
    c: Vertical(g0)
    c: Vertical(g2)
    c: Symmetric(g1,g0,g4)
    c: PointOnObject(g4,g-1)
    c: DistanceX(g-3,g4) = 20
    c: DistanceX(g1,g1) = 10
    c: DistanceY(g2,g2) = 14
FEATURE [Sketcher::SketchObject] Sketch011  label="SketchStandoffBottom"
  ExternalGeometry = -> [Sketch010]
  FullyConstrained = true
  MapMode = 5
  Placement = pos=(7,-56.2806,48.4148) rot=(1,0,0;3.14159rad)
  Support = -> [DatumPlane008]
  expr: Constraints[14] = <<s>>.y_standoff_klein
  expr: Constraints[15] = <<s>>.x_standoff_klein
  sketch-geometry (7):
    g0: LineSegment StartX=-7 StartY=-15 StartZ=0 EndX=7 EndY=-25 EndZ=0
    g1: GeomPoint X=0 Y=-20 Z=0
    g2: LineSegment StartX=-6 StartY=-16 StartZ=0 EndX=-6 EndY=-24 EndZ=0
    g3: LineSegment StartX=-6 StartY=-24 StartZ=0 EndX=6 EndY=-24 EndZ=0
    g4: LineSegment StartX=6 StartY=-24 StartZ=0 EndX=6 EndY=-16 EndZ=0
    g5: LineSegment StartX=6 StartY=-16 StartZ=0 EndX=-6 EndY=-16 EndZ=0
    g6: GeomPoint X=0 Y=-20 Z=0
  constraints (16):
    c: Coincident(g0,g-3)
    c: Coincident(g0,g-4)
    c: PointOnObject(g1,g0)
    c: Vertical(g-1,g1)
    c: Coincident(g2,g3)
    c: Coincident(g3,g4)
    c: Coincident(g4,g5)
    c: Coincident(g5,g2)
    c: Horizontal(g3)
    c: Horizontal(g5)
    c: Vertical(g2)
    c: Vertical(g4)
    c: Symmetric(g3,g2,g6)
    c: Coincident(g6,g1)
    c: DistanceY(g4,g4) = 8
    c: DistanceX(g5,g5) = 12
FEATURE [PartDesign::AdditiveLoft] AdditiveLoft
  BaseFeature = -> Pad006
  Closed = false
  Placement = pos=(7,-1.98e-14,53.4148) rot=(0.707107,0.707107,0;3.14159rad)
  Profile = -> Sketch011
  Ruled = false
  Sections = -> [Sketch010]
FEATURE [PartDesign::Plane] DatumPlane009  label="DatumPlanePockets"
  Length = 60
  MapMode = 5
  Placement = pos=(7,-1.98e-14,53.4148) rot=(0,0,1;1.5708rad)
  ResizeMode = 0
  Support = -> [AdditiveLoft]
  Width = 60
FEATURE [Sketcher::SketchObject] Sketch012  label="SketchSchraubenPockets"
  ExternalGeometry = -> [Sketch009]
  FullyConstrained = true
  MapMode = 5
  Placement = pos=(7,-1.98e-14,53.4148) rot=(0,0,1;1.5708rad)
  Support = -> [DatumPlane009]
  expr: Constraints[2] = <<s>>.y_wz_abstand_loecher / 2
  expr: Constraints[3] = <<s>>.durchmesser_wz_loecher_gross
  expr: Constraints[4] = <<s>>.x_wz_abstand_loecher
  sketch-geometry (2):
    g0: Circle CenterX=-36.2806 CenterY=3 CenterZ=0 NormalX=0 NormalY=0 NormalZ=1 AngleXU=0 Radius=1.75
    g1: Circle CenterX=-36.2806 CenterY=-3 CenterZ=0 NormalX=0 NormalY=0 NormalZ=1 AngleXU=0 Radius=1.75
  constraints (5):
    c: Equal(g0,g1)
    c: Symmetric(g0,g1,g-1)
    c: DistanceX(g-3,g0) = 20
    c: Diameter(g1) = 3.5
    c: DistanceY(g1,g0) = 6
FEATURE [PartDesign::Pocket] Pocket003  label="PocketSchrauben"
  BaseFeature = -> AdditiveLoft
  Direction = (-8e-16,1.1e-15,-1)
  Length = 5
  Length2 = 5
  Placement = pos=(7,-1.98e-14,53.4148) rot=(0.707107,0.707107,0;3.14159rad)
  Profile = -> Sketch012
  ReferenceAxis = -> Sketch012 [N_Axis]
  Type = 1
FEATURE [Sketcher::SketchObject] Sketch013
  ExternalGeometry = -> [Pocket003]
  FullyConstrained = true
  MapMode = 5
  Placement = pos=(7,-1.98e-14,53.4148) rot=(0,0,1;1.5708rad)
  Support = -> [DatumPlane009]
  expr: Constraints[3] = <<s>>.durchmesser_m3_schraube_kopf + <<s>>.spalt_pocket_schraubenkopf
  sketch-geometry (2):
    g0: Circle CenterX=-36.2806 CenterY=3 CenterZ=0 NormalX=0 NormalY=0 NormalZ=1 AngleXU=0 Radius=2.9
    g1: Circle CenterX=-36.2806 CenterY=-3 CenterZ=0 NormalX=0 NormalY=0 NormalZ=1 AngleXU=0 Radius=2.9
  constraints (4):
    c: Coincident(g0,g-3)
    c: Coincident(g1,g-4)
    c: Equal(g1,g0)
    c: Diameter(g0) = 5.8
FEATURE [PartDesign::Pocket] Pocket004  label="PocketSchraubenKopf"
  BaseFeature = -> Pocket003
  Direction = (-8e-16,1.1e-15,-1)
  Length = 3.2
  Length2 = 5
  Placement = pos=(7,-1.98e-14,53.4148) rot=(0.707107,0.707107,0;3.14159rad)
  Profile = -> Sketch013
  ReferenceAxis = -> Sketch013 [N_Axis]
  Type = 0
  expr: Length = <<s>>.z_m3_schraube_kopf
FEATURE [PartDesign::Body] Body004  label="BasePlateWaage"
  Group = -> [ShapeBinder005,DatumPlane006,Sketch009,Pad006,DatumPlane007,DatumPlane008,Sketch010,Sketch011,AdditiveLoft,DatumPlane009,Sketch012,Pocket003,Sketch013,Pocket004]
  Origin = -> Origin004
  Tip = -> Pocket004
FEATURE [PartDesign::ShapeBinder] ShapeBinder006
  Placement = pos=(7,-1.98e-14,53.4148) rot=(0.707107,0.707107,0;3.14159rad)
  Support = -> [Pocket004]
  TraceSupport = false
FEATURE [PartDesign::Plane] DatumPlane010  label="DatumPlaneWaegeZelle"
  Length = 60
  MapMode = 5
  Placement = pos=(7,-1.07e-14,48.4148) rot=(0.707107,0.707107,0;3.14159rad)
  ResizeMode = 0
  Support = -> [ShapeBinder006]
  Width = 60
FEATURE [Sketcher::SketchObject] Sketch014  label="SketchWZ"
  ExternalGeometry = -> [ShapeBinder006]
  FullyConstrained = true
  MapMode = 5
  Placement = pos=(7,-1.07e-14,48.4148) rot=(0.707107,0.707107,0;3.14159rad)
  Support = -> [DatumPlane010]
  expr: Constraints[37] = <<s>>.y_wz_gesamt
  expr: Constraints[38] = <<s>>.y_wz_kurz
  expr: Constraints[39] = <<s>>.x_wz_max
  expr: Constraints[40] = <<s>>.x_wz_min
  sketch-geometry (15):
    g0: LineSegment StartX=-32.5306 StartY=6 StartZ=0 EndX=-40.0306 EndY=6 EndZ=0
    g1: LineSegment StartX=-40.0306 StartY=6 StartZ=0 EndX=-40.0306 EndY=3.5 EndZ=0
    g2: LineSegment StartX=-40.0306 StartY=3.5 StartZ=0 EndX=-72.0306 EndY=3.5 EndZ=0
    g3: LineSegment StartX=-72.0306 StartY=3.5 StartZ=0 EndX=-72.0306 EndY=6 EndZ=0
    g4: LineSegment StartX=-72.0306 StartY=6 StartZ=0 EndX=-79.5306 EndY=6 EndZ=0
    g5: LineSegment StartX=-79.5306 StartY=6 StartZ=0 EndX=-79.5306 EndY=-6 EndZ=0
    g6: LineSegment StartX=-79.5306 StartY=-6 StartZ=0 EndX=-72.0306 EndY=-6 EndZ=0
    g7: LineSegment StartX=-72.0306 StartY=-6 StartZ=0 EndX=-72.0306 EndY=-3.5 EndZ=0
    g8: LineSegment StartX=-72.0306 StartY=-3.5 StartZ=0 EndX=-40.0306 EndY=-3.5 EndZ=0
    g9: LineSegment StartX=-40.0306 StartY=-3.5 StartZ=0 EndX=-40.0306 EndY=-6 EndZ=0
    g10: LineSegment StartX=-40.0306 StartY=-6 StartZ=0 EndX=-32.5306 EndY=-6 EndZ=0
    g11: LineSegment StartX=-32.5306 StartY=-6 StartZ=0 EndX=-32.5306 EndY=6 EndZ=0
    g12: LineSegment StartX=-40.0306 StartY=6 StartZ=0 EndX=-32.5306 EndY=-6 EndZ=0
    g13: LineSegment StartX=-40.0306 StartY=-6 StartZ=0 EndX=-32.5306 EndY=6 EndZ=0
    g14: GeomPoint X=-36.2806 Y=-2.5e-15 Z=0
  constraints (41):
    c: Horizontal(g0)
    c: Coincident(g0,g1)
    c: Vertical(g1)
    c: Coincident(g1,g2)
    c: Horizontal(g2)
    c: Coincident(g2,g3)
    c: Vertical(g3)
    c: Coincident(g3,g4)
    c: Horizontal(g4)
    c: Coincident(g4,g5)
    c: Vertical(g5)
    c: Coincident(g5,g6)
    c: Horizontal(g6)
    c: Coincident(g6,g7)
    c: Vertical(g7)
    c: Coincident(g7,g8)
    c: Horizontal(g8)
    c: Coincident(g8,g9)
    c: Vertical(g9)
    c: Coincident(g9,g10)
    c: Horizontal(g10)
    c: Coincident(g10,g11)
    c: Coincident(g11,g0)
    c: Vertical(g11)
    c: Vertical(g1,g8)
    c: Equal(g4,g0)
    c: Horizontal(g3,g0)
    c: Horizontal(g6,g9)
    c: Symmetric(g2,g7,g-1)
    c: Equal(g7,g3)
    c: Coincident(g12,g0)
    c: Coincident(g12,g10)
    c: Coincident(g13,g9)
    c: Coincident(g13,g0)
    c: PointOnObject(g14,g12)
    c: PointOnObject(g14,g13)
    c: Vertical(g14,g-3)
    c: DistanceX(g5,g10) = 47
    c: DistanceX(g10,g10) = 7.5
    c: DistanceY(g11,g11) = 12
    c: DistanceY(g8,g1) = 7
FEATURE [PartDesign::Pad] Pad007
  Direction = (-1.5e-15,1.8e-15,-1)
  Length = 6
  Length2 = 10
  Placement = pos=(7,-1.07e-14,48.4148) rot=(0.707107,0.707107,0;3.14159rad)
  Profile = -> Sketch014
  ReferenceAxis = -> Sketch014 [N_Axis]
  Type = 0
  expr: Length = <<s>>.z_wz_pad
FEATURE [PartDesign::Plane] DatumPlane011  label="DatumPlaneWZPockets"
  Length = 60
  MapMode = 5
  Placement = pos=(7,-1.07e-14,48.4148) rot=(0,0,1;1.5708rad)
  ResizeMode = 0
  Support = -> [Pad007]
  Width = 60
FEATURE [Sketcher::SketchObject] Sketch015  label="SketchPocketsSchrauben"
  ExternalGeometry = -> [ShapeBinder006,Sketch014]
  FullyConstrained = true
  MapMode = 5
  Placement = pos=(7,-1.07e-14,48.4148) rot=(0,0,1;1.5708rad)
  Support = -> [DatumPlane011]
  expr: Constraints[15] = <<s>>.durchmesser_wz_loecher_klein
  sketch-geometry (8):
    g0: Circle CenterX=-36.2806 CenterY=3 CenterZ=0 NormalX=0 NormalY=0 NormalZ=1 AngleXU=0 Radius=1.75
    g1: Circle CenterX=-36.2806 CenterY=-3 CenterZ=0 NormalX=0 NormalY=0 NormalZ=1 AngleXU=0 Radius=1.75
    g2: LineSegment StartX=-72.0306 StartY=3.5 StartZ=0 EndX=-40.0306 EndY=-3.5 EndZ=0
    g3: LineSegment StartX=-40.0306 StartY=3.5 StartZ=0 EndX=-72.0306 EndY=-3.5 EndZ=0
    g4: GeomPoint X=-56.0306 Y=2e-16 Z=0
    g5: LineSegment StartX=-56.0306 StartY=2e-16 StartZ=0 EndX=-56.0306 EndY=3.5 EndZ=0
    g6: Circle CenterX=-75.7806 CenterY=3 CenterZ=0 NormalX=0 NormalY=0 NormalZ=1 AngleXU=0 Radius=1.5
    g7: Circle CenterX=-75.7806 CenterY=-3 CenterZ=0 NormalX=0 NormalY=0 NormalZ=1 AngleXU=0 Radius=1.5
  constraints (17):
    c: Coincident(g0,g-3)
    c: Coincident(g1,g-4)
    c: Equal(g1,g-4)
    c: Equal(g1,g0)
    c: Coincident(g2,g-5)
    c: Coincident(g2,g-6)
    c: Coincident(g3,g-5)
    c: Coincident(g3,g-6)
    c: PointOnObject(g4,g3)
    c: PointOnObject(g4,g2)
    c: Coincident(g5,g4)
    c: PointOnObject(g5,g-5)
    c: Vertical(g5)
    c: Symmetric(g6,g7,g-1)
    c: Equal(g6,g7)
    c: Diameter(g6) = 3
    c: Symmetric(g6,g0,g5)
FEATURE [PartDesign::Pocket] Pocket005
  BaseFeature = -> Pad007
  Direction = (-1.9e-15,2e-15,-1)
  Length = 5
  Length2 = 5
  Placement = pos=(7,-1.07e-14,48.4148) rot=(0.707107,0.707107,0;3.14159rad)
  Profile = -> Sketch015
  ReferenceAxis = -> Sketch015 [N_Axis]
  Type = 1
FEATURE [PartDesign::Plane] DatumPlane012
  Length = 62.1173
  MapMode = 5
  Placement = pos=(10.5,-1.15e-14,48.4148) rot=(-0.57735,0.57735,-0.57735;2.0944rad)
  ResizeMode = 0
  Support = -> [Pocket005]
  Width = 85.5321
FEATURE [Sketcher::SketchObject] Sketch016  label="SketchSlot"
  ExternalGeometry = -> [Pocket005,Sketch014]
  FullyConstrained = true
  MapMode = 5
  Placement = pos=(10.5,-1.15e-14,48.4148) rot=(-0.57735,0.57735,-0.57735;2.0944rad)
  Support = -> [DatumPlane012]
  expr: Constraints[19] = <<s>>.y_laenge_wz_slot
  expr: Constraints[26] = <<s>>.durchmesser_wz_bohrung
  expr: Constraints[9] = <<s>>.z_hoehe_wz_slot
  sketch-geometry (11):
    g0: LineSegment StartX=48.1956 StartY=4.25 StartZ=0 EndX=63.8655 EndY=4.25 EndZ=0
    g1: LineSegment StartX=48.1956 StartY=1.75 StartZ=0 EndX=63.8655 EndY=1.75 EndZ=0
    g2: LineSegment StartX=48.1956 StartY=4.25 StartZ=0 EndX=63.8655 EndY=1.75 EndZ=0
    g3: LineSegment StartX=48.1956 StartY=1.75 StartZ=0 EndX=63.8655 EndY=4.25 EndZ=0
    g4: GeomPoint X=56.0306 Y=3 Z=0
    g5: LineSegment StartX=40.0306 StartY=0 StartZ=0 EndX=72.0306 EndY=6 EndZ=0
    g6: LineSegment StartX=72.0306 StartY=0 StartZ=0 EndX=40.0306 EndY=6 EndZ=0
    g7: GeomPoint X=43.5306 Y=3 Z=0
    g8: GeomPoint X=68.5306 Y=3 Z=0
    g9: ArcOfCircle CenterX=46.0306 CenterY=3 CenterZ=0 NormalX=0 NormalY=0 NormalZ=1 AngleXU=0 Radius=2.5 StartAngle=0.523599 EndAngle=5.75959
    g10: ArcOfCircle CenterX=66.0306 CenterY=3 CenterZ=0 NormalX=0 NormalY=0 NormalZ=1 AngleXU=0 Radius=2.5 StartAngle=3.66519 EndAngle=8.90118
  constraints (28):
    c: Horizontal(g0)
    c: Horizontal(g1)
    c: Vertical(g0,g1)
    c: Vertical(g0,g1)
    c: Coincident(g2,g0)
    c: Coincident(g2,g1)
    c: Coincident(g3,g1)
    c: Coincident(g3,g0)
    c: PointOnObject(g4,g2)
    c: DistanceY(g1,g0) = 2.5
    c: Coincident(g5,g-4)
    c: Coincident(g5,g-3)
    c: Coincident(g6,g-4)
    c: Coincident(g6,g-3)
    c: PointOnObject(g4,g3)
    c: PointOnObject(g4,g6)
    c: PointOnObject(g4,g5)
    c: Horizontal(g8,g4)
    c: Horizontal(g4,g7)
    c: DistanceX(g7,g8) = 25
    c: Coincident(g9,g0)
    c: Coincident(g9,g1)
    c: PointOnObject(g7,g9)
    c: Coincident(g10,g0)
    c: Coincident(g10,g1)
    c: PointOnObject(g8,g10)
    c: Diameter(g9) = 5
    c: Equal(g9,g10)
FEATURE [PartDesign::Pocket] Pocket006  label="PocketWZ"
  BaseFeature = -> Pocket005
  Direction = (-1,4e-16,1.8e-15)
  Length = 5
  Length2 = 5
  Placement = pos=(7,-1.07e-14,48.4148) rot=(0.707107,0.707107,0;3.14159rad)
  Profile = -> Sketch016
  ReferenceAxis = -> Sketch016 [N_Axis]
  Type = 1
FEATURE [PartDesign::Body] Body005  label="WaegeZelle"
  Group = -> [ShapeBinder006,DatumPlane010,Sketch014,Pad007,DatumPlane011,Sketch015,Pocket005,DatumPlane012,Sketch016,Pocket006]
  Origin = -> Origin005
  Tip = -> Pocket006
FEATURE [PartDesign::ShapeBinder] ShapeBinder007  label="ShapeBinderWZ"
  Placement = pos=(7,-1.07e-14,48.4148) rot=(0.707107,0.707107,0;3.14159rad)
  Support = -> [Pocket006]
  TraceSupport = false
FEATURE [PartDesign::Plane] DatumPlane013  label="DatumPlaneStandoffTeilTop"
  Length = 132.926
  MapMode = 5
  Placement = pos=(7,3.6e-15,42.4148) rot=(0.707107,0.707107,0;3.14159rad)
  ResizeMode = 0
  Support = -> [ShapeBinder007]
  Width = 145.146
FEATURE [Sketcher::SketchObject] Sketch017  label="SketchStandoffTeilTop"
  ExternalGeometry = -> [ShapeBinder007]
  FullyConstrained = true
  MapMode = 5
  Placement = pos=(7,3.6e-15,42.4148) rot=(0.707107,0.707107,0;3.14159rad)
  Support = -> [DatumPlane013]
  expr: Constraints[11] = <<s>>.y_standoff_klein
  expr: Constraints[12] = <<s>>.x_standoff_klein
  sketch-geometry (5):
    g0: LineSegment StartX=-71.7806 StartY=6 StartZ=0 EndX=-71.7806 EndY=-6 EndZ=0
    g1: LineSegment StartX=-71.7806 StartY=-6 StartZ=0 EndX=-79.7806 EndY=-6 EndZ=0
    g2: LineSegment StartX=-79.7806 StartY=-6 StartZ=0 EndX=-79.7806 EndY=6 EndZ=0
    g3: LineSegment StartX=-79.7806 StartY=6 StartZ=0 EndX=-71.7806 EndY=6 EndZ=0
    g4: GeomPoint X=-75.7806 Y=0 Z=0
  constraints (13):
    c: Coincident(g0,g1)
    c: Coincident(g1,g2)
    c: Coincident(g2,g3)
    c: Coincident(g3,g0)
    c: Horizontal(g1)
    c: Horizontal(g3)
    c: Vertical(g0)
    c: Vertical(g2)
    c: Symmetric(g1,g0,g4)
    c: Vertical(g4,g-3)
    c: PointOnObject(g4,g-1)
    c: DistanceX(g3,g3) = 8
    c: DistanceY(g2,g2) = 12
FEATURE [PartDesign::Plane] DatumPlane014  label="DatumPlaneStandoffTeilBottom"
  AttachmentOffset = pos=(0,0,5) rot=(0,0,1;0rad)
  Length = 132.926
  MapMode = 5
  Placement = pos=(7,1.55e-14,37.4148) rot=(0.707107,0.707107,0;3.14159rad)
  ResizeMode = 0
  Support = -> [ShapeBinder007]
  Width = 145.146
  expr: .AttachmentOffset.Base.z = Spreadsheet.z_standoff_hoehe_am_teil
FEATURE [Sketcher::SketchObject] Sketch018  label="SketchStandoffTeilBottom"
  ExternalGeometry = -> [ShapeBinder007]
  FullyConstrained = true
  MapMode = 5
  Placement = pos=(7,1.55e-14,37.4148) rot=(0.707107,0.707107,0;3.14159rad)
  Support = -> [DatumPlane014]
  expr: Constraints[11] = <<s>>.y_standoff_gross
  expr: Constraints[12] = <<s>>.x_standoff_gross
  sketch-geometry (5):
    g0: LineSegment StartX=-80.7806 StartY=7 StartZ=0 EndX=-80.7806 EndY=-7 EndZ=0
    g1: LineSegment StartX=-80.7806 StartY=-7 StartZ=0 EndX=-70.7806 EndY=-7 EndZ=0
    g2: LineSegment StartX=-70.7806 StartY=-7 StartZ=0 EndX=-70.7806 EndY=7 EndZ=0
    g3: LineSegment StartX=-70.7806 StartY=7 StartZ=0 EndX=-80.7806 EndY=7 EndZ=0
    g4: GeomPoint X=-75.7806 Y=0 Z=0
  constraints (13):
    c: Coincident(g0,g1)
    c: Coincident(g1,g2)
    c: Coincident(g2,g3)
    c: Coincident(g3,g0)
    c: Horizontal(g1)
    c: Horizontal(g3)
    c: Vertical(g0)
    c: Vertical(g2)
    c: Symmetric(g1,g0,g4)
    c: PointOnObject(g4,g-1)
    c: Vertical(g4,g-3)
    c: DistanceX(g3,g3) = 10
    c: DistanceY(g0,g0) = 14
FEATURE [PartDesign::AdditiveLoft] AdditiveLoft001  label="StandoffAmTeil"
  Closed = false
  Placement = pos=(7,1.55e-14,37.4148) rot=(0.707107,0.707107,0;3.14159rad)
  Profile = -> Sketch018
  Ruled = false
  Sections = -> [Sketch017]
FEATURE [Sketcher::SketchObject] Sketch019  label="SketchAdapterDuplicate"
  ExternalGeometry = -> [ShapeBinder008,Sketch018]
  FullyConstrained = true
  MapMode = 5
  Support = -> [XY_Plane006]
  expr: Constraints[29] = <<s>>.y_abstand_standoff_vorderseite
  sketch-geometry (14):
    g0: LineSegment StartX=-51 StartY=-63 StartZ=0 EndX=-51 EndY=-27.5 EndZ=0
    g1: LineSegment StartX=-51 StartY=-27.5 StartZ=0 EndX=-61 EndY=-27.5 EndZ=0
    g2: LineSegment StartX=-61 StartY=-27.5 StartZ=0 EndX=-61 EndY=-84.7806 EndZ=0
    g3: LineSegment StartX=61 StartY=-84.7806 StartZ=0 EndX=61 EndY=-27.5 EndZ=0
    g4: LineSegment StartX=61 StartY=-27.5 StartZ=0 EndX=51 EndY=-27.5 EndZ=0
    g5: LineSegment StartX=51 StartY=-27.5 StartZ=0 EndX=51 EndY=-63 EndZ=0
    g6: LineSegment StartX=51 StartY=-63 StartZ=0 EndX=34.5 EndY=-63 EndZ=0
    g7: LineSegment StartX=34.5 StartY=-63 StartZ=0 EndX=34.5 EndY=-27.5 EndZ=0
    g8: ArcOfCircle CenterX=28.5 CenterY=-27.5 CenterZ=0 NormalX=0 NormalY=0 NormalZ=1 AngleXU=0 Radius=6 StartAngle=-9e-16 EndAngle=1.5708
    g9: LineSegment StartX=28.5 StartY=-21.5 StartZ=0 EndX=-14.5 EndY=-21.5 EndZ=0
    g10: ArcOfCircle CenterX=-14.5 CenterY=-27.5 CenterZ=0 NormalX=0 NormalY=0 NormalZ=1 AngleXU=0 Radius=6 StartAngle=1.5708 EndAngle=3.14159
    g11: LineSegment StartX=-20.5 StartY=-27.5 StartZ=0 EndX=-20.5 EndY=-63 EndZ=0
    g12: LineSegment StartX=-20.5 StartY=-63 StartZ=0 EndX=-51 EndY=-63 EndZ=0
    g13: LineSegment StartX=-61 StartY=-84.7806 StartZ=0 EndX=61 EndY=-84.7806 EndZ=0
  constraints (30):
    c: Coincident(g0,g1)
    c: Coincident(g1,g2)
    c: Coincident(g3,g4)
    c: Coincident(g4,g5)
    c: Coincident(g5,g6)
    c: Coincident(g6,g7)
    c: Tangent(g7,g8) = -1.5708
    c: Coincident(g8,g9)
    c: Tangent(g9,g10) = -1.5708
    c: Coincident(g10,g11)
    c: Coincident(g11,g12)
    c: Coincident(g12,g0)
    c: Vertical(g3)
    c: Vertical(g2)
    c: Coincident(g13,g2)
    c: Coincident(g13,g3)
    c: Horizontal(g13)
    c: Coincident(g1,g-4)
    c: Coincident(g-16,g0)
    c: Coincident(g0,g-16)
    c: Coincident(g11,g-15)
    c: Coincident(g10,g-13)
    c: Coincident(g10,g-14)
    c: Coincident(g8,g-12)
    c: Coincident(g7,g-11)
    c: Coincident(g6,g-10)
    c: Coincident(g5,g-9)
    c: Coincident(g4,g-8)
    c: Coincident(g3,g-7)
    c: DistanceY(g2,g-17) = 4
FEATURE [PartDesign::Pad] Pad008  label="PadAdapterDuplicate"
  BaseFeature = -> AdditiveLoft001
  Direction = (0,0,1)
  Length = 10
  Length2 = 10
  Placement = pos=(7,1.55e-14,37.4148) rot=(0.707107,0.707107,0;3.14159rad)
  Profile = -> Sketch019
  ReferenceAxis = -> Sketch019 [N_Axis]
  Type = 3
  UpToFace = -> AdditiveLoft001 [Face1]
FEATURE [Sketcher::SketchObject] Sketch020
  ExternalGeometry = -> [Sketch018,ShapeBinder008]
  FullyConstrained = true
  MapMode = 5
  Support = -> [XY_Plane006]
  expr: Constraints[11] = <<s>>.wandstaerke_pocket_mitte
  expr: Constraints[12] = <<s>>.wandstaerke_pocket_mitte
  expr: Constraints[14] = <<s>>.wandstaerke_pocket_mitte
  expr: Constraints[1] = <<s>>.wandstaerke_pocket_mitte
  expr: Constraints[22] = <<s>>.wandstaerke_pocket_mitte
  expr: Constraints[23] = <<s>>.wandstaerke_pocket_mitte
  expr: Constraints[2] = <<s>>.wandstaerke_pocket_mitte
  expr: Constraints[32] = <<s>>.wandstaerke_pocket_mitte
  sketch-geometry (14):
    g0: LineSegment StartX=-18.5 StartY=-27.5 StartZ=0 EndX=-18.5 EndY=-65 EndZ=0
    g1: LineSegment StartX=-59 StartY=-29.5 StartZ=0 EndX=-59 EndY=-80.7806 EndZ=0
    g2: LineSegment StartX=-59 StartY=-80.7806 StartZ=0 EndX=59 EndY=-80.7806 EndZ=0
    g3: LineSegment StartX=59 StartY=-80.7806 StartZ=0 EndX=59 EndY=-29.5 EndZ=0
    g4: LineSegment StartX=32.5 StartY=-65 StartZ=0 EndX=32.5 EndY=-27.5 EndZ=0
    g5: LineSegment StartX=-59 StartY=-29.5 StartZ=0 EndX=-53 EndY=-29.5 EndZ=0
    g6: LineSegment StartX=-53 StartY=-29.5 StartZ=0 EndX=-53 EndY=-65 EndZ=0
    g7: LineSegment StartX=-53 StartY=-65 StartZ=0 EndX=-18.5 EndY=-65 EndZ=0
    g8: LineSegment StartX=59 StartY=-29.5 StartZ=0 EndX=53 EndY=-29.5 EndZ=0
    g9: LineSegment StartX=53 StartY=-29.5 StartZ=0 EndX=53 EndY=-65 EndZ=0
    g10: LineSegment StartX=53 StartY=-65 StartZ=0 EndX=32.5 EndY=-65 EndZ=0
    g11: ArcOfCircle CenterX=-14.5 CenterY=-27.5 CenterZ=0 NormalX=0 NormalY=0 NormalZ=1 AngleXU=0 Radius=4 StartAngle=1.5708 EndAngle=3.14159
    g12: LineSegment StartX=-14.5 StartY=-23.5 StartZ=0 EndX=28.5 EndY=-23.5 EndZ=0
    g13: ArcOfCircle CenterX=28.5 CenterY=-27.5 CenterZ=0 NormalX=0 NormalY=0 NormalZ=1 AngleXU=0 Radius=4 StartAngle=-9.635e-12 EndAngle=1.5708
  constraints (42):
    c: Horizontal(g0,g-4)
    c: DistanceX(g-4,g0) = 2
    c: DistanceX(g4,g-5) = 2
    c: Horizontal(g-3,g2)
    c: Vertical(g0)
    c: Vertical(g1)
    c: Coincident(g1,g2)
    c: Horizontal(g2)
    c: Vertical(g3)
    c: Vertical(g4)
    c: Horizontal(g4,g0)
    c: DistanceX(g-6,g1) = 2
    c: DistanceX(g3,g-7) = 2
    c: Coincident(g2,g3)
    c: DistanceY(g1,g-6) = 2
    c: Coincident(g5,g1)
    c: Horizontal(g5)
    c: Coincident(g5,g6)
    c: Vertical(g6)
    c: Coincident(g6,g7)
    c: Coincident(g7,g0)
    c: Horizontal(g7)
    c: DistanceX(g5,g-8) = 2
    c: DistanceY(g6,g-8) = 2
    c: Horizontal(g3,g5)
    c: Coincident(g3,g8)
    c: Horizontal(g8)
    c: Coincident(g8,g9)
    c: Vertical(g9)
    c: Coincident(g9,g10)
    c: Coincident(g10,g4)
    c: Horizontal(g10)
    c: DistanceX(g-9,g8) = 2
    c: Coincident(g11,g-10)
    c: Coincident(g11,g0)
    c: Coincident(g12,g11)
    c: Horizontal(g12)
    c: Coincident(g13,g-11)
    c: Coincident(g13,g4)
    c: Coincident(g13,g12)
    c: Vertical(g11,g-10)
    c: Vertical(g12,g-11)
FEATURE [PartDesign::Pocket] Pocket007  label="PocketGrossMitte"
  BaseFeature = -> Pad008
  Direction = (0,0,-1)
  Length = 0
  Length2 = 5
  Offset = 2
  Placement = pos=(7,1.55e-14,37.4148) rot=(0.707107,0.707107,0;3.14159rad)
  Profile = -> Sketch020
  ReferenceAxis = -> Sketch020 [N_Axis]
  Type = 3
  UpToFace = -> Pad008 [Face4]
  expr: Offset = <<s>>.wandstaerke_pocket_mitte
FEATURE [Sketcher::SketchObject] Sketch021  label="SketchPocketWZ"
  ExternalGeometry = -> [ShapeBinder007]
  FullyConstrained = true
  MapMode = 5
  Placement = pos=(7,3.6e-15,42.4148) rot=(0.707107,0.707107,0;3.14159rad)
  Support = -> [DatumPlane013]
  expr: Constraints[3] = <<s>>.m3_bohrung
  sketch-geometry (2):
    g0: Circle CenterX=-75.7806 CenterY=3 CenterZ=0 NormalX=0 NormalY=0 NormalZ=1 AngleXU=0 Radius=2
    g1: Circle CenterX=-75.7806 CenterY=-3 CenterZ=0 NormalX=0 NormalY=0 NormalZ=1 AngleXU=0 Radius=2
  constraints (4):
    c: Coincident(g0,g-3)
    c: Coincident(g1,g-4)
    c: Equal(g0,g1)
    c: Diameter(g0) = 4
FEATURE [PartDesign::Pocket] Pocket008  label="PocketSchraubenWZ"
  BaseFeature = -> Pocket007
  Direction = (2.3e-15,-2.4e-15,1)
  Length = 5
  Length2 = 5
  Placement = pos=(7,1.55e-14,37.4148) rot=(0.707107,0.707107,0;3.14159rad)
  Profile = -> Sketch021
  ReferenceAxis = -> Sketch021 [N_Axis]
  Reversed = true
  Type = 1
FEATURE [PartDesign::Plane] DatumPlane015  label="DatumPlaneThreadedInserts"
  AttachmentOffset = pos=(0,0,0) rot=(0,0,-1;3.14159rad)
  Length = 140.138
  MapMode = 5
  Placement = pos=(7,-84.7806,37.4148) rot=(-1,0,0;4.71239rad)
  ResizeMode = 0
  Support = -> [Pocket008]
  Width = 85.5527
FEATURE [Sketcher::SketchObject] Sketch022  label="SketchThreadedInserts"
  ExternalGeometry = -> [ShapeBinder008,ShapeBinder007]
  FullyConstrained = true
  MapMode = 5
  Placement = pos=(7,-84.7806,37.4148) rot=(1,0,0;1.5708rad)
  Support = -> [DatumPlane015]
  expr: Constraints[7] = <<s>>.m2_bohrung
  expr: Constraints[8] = <<s>>.x_abstand_threaded_inserts
  expr: Constraints[9] = <<s>>.z_abstand_threaded_inserts
  sketch-geometry (12):
    g0: Circle CenterX=-32.5 CenterY=-5.70738 CenterZ=0 NormalX=0 NormalY=0 NormalZ=1 AngleXU=0 Radius=0.9
    g1: Circle CenterX=32.5 CenterY=-5.70738 CenterZ=0 NormalX=0 NormalY=0 NormalZ=1 AngleXU=0 Radius=0.9
    g2: Circle CenterX=-32.5 CenterY=-31.7074 CenterZ=0 NormalX=0 NormalY=0 NormalZ=1 AngleXU=0 Radius=0.9
    g3: Circle CenterX=32.5 CenterY=-31.7074 CenterZ=0 NormalX=0 NormalY=0 NormalZ=1 AngleXU=0 Radius=0.9
    g4: LineSegment StartX=-32.5 StartY=-31.7074 StartZ=0 EndX=-32.5 EndY=-37.4148 EndZ=0
    g5: LineSegment StartX=-32.5 StartY=-5.70738 StartZ=0 EndX=-32.5 EndY=0 EndZ=0
    g6: LineSegment StartX=-32.5 StartY=-5.70738 StartZ=0 EndX=32.5 EndY=-31.7074 EndZ=0
    g7: LineSegment StartX=32.5 StartY=-5.70738 StartZ=0 EndX=-32.5 EndY=-31.7074 EndZ=0
    g8: GeomPoint X=-1.35e-14 Y=-18.7074 Z=0
    g9: Circle CenterX=-6 CenterY=5 CenterZ=0 NormalX=0 NormalY=0 NormalZ=1 AngleXU=0 Radius=12
    g10: Circle CenterX=6 CenterY=5 CenterZ=0 NormalX=0 NormalY=0 NormalZ=1 AngleXU=0 Radius=12
    g11: GeomPoint X=-1.35e-14 Y=15.3923 Z=0
  constraints (30):
    c: Equal(g0,g1)
    c: Equal(g1,g3)
    c: Equal(g3,g2)
    c: Horizontal(g0,g1)
    c: Horizontal(g2,g3)
    c: Vertical(g0,g2)
    c: Vertical(g1,g3)
    c: Diameter(g1) = 1.8
    c: DistanceX(g0,g1) = 65
    c: DistanceY(g2,g0) = 26
    c: Coincident(g4,g2)
    c: PointOnObject(g4,g-3)
    c: Vertical(g4)
    c: Coincident(g5,g0)
    c: Horizontal(g5,g-1)
    c: Vertical(g5)
    c: Equal(g4,g5)
    c: Coincident(g6,g0)
    c: Coincident(g6,g3)
    c: Coincident(g7,g1)
    c: Coincident(g7,g2)
    c: PointOnObject(g8,g6)
    c: PointOnObject(g8,g7)
    c: Coincident(g9,g-4)
    c: PointOnObject(g-4,g9)
    c: Coincident(g10,g-4)
    c: PointOnObject(g9,g10)
    c: PointOnObject(g11,g9)
    c: PointOnObject(g11,g10)
    c: Vertical(g11,g8)
FEATURE [PartDesign::Pocket] Pocket009  label="PocketThreadedInserts"
  BaseFeature = -> Pocket008
  Direction = (-2e-16,1,4e-16)
  Length = 5
  Length2 = 5
  Placement = pos=(7,1.55e-14,37.4148) rot=(0.707107,0.707107,0;3.14159rad)
  Profile = -> Sketch022
  ReferenceAxis = -> Sketch022 [N_Axis]
  Type = 2
FEATURE [Part::FeaturePython] Screw004  label="M3x14-Screw"  # Fasteners workbench fastener (typed FeaturePython)
  Placement = pos=(4,-75.7806,35.4148) rot=(0.707107,0.707107,0;3.14159rad)
  baseObject = -> Body006 [Edge92]
  diameter = 4
  invert = true
  leftHanded = false
  length = 5
  lengthCustom = 14
  matchOuter = true
  offset = 0
  thread = true
  type = 48
FEATURE [PartDesign::Plane] DatumPlane016
  AttachmentOffset = pos=(0,0,0) rot=(0,0,1;3.14159rad)
  Length = 126.986
  MapMode = 5
  Placement = pos=(51,1.55e-14,37.4148) rot=(-0.57735,0.57735,0.57735;4.18879rad)
  ResizeMode = 0
  Support = -> [Pocket009]
  Width = 84.6204
FEATURE [Sketcher::SketchObject] Sketch023
  ExternalGeometry = -> [Pocket009,Sketch019]
  FullyConstrained = true
  MapMode = 5
  Placement = pos=(51,1.55e-14,37.4148) rot=(-0.57735,0.57735,0.57735;4.18879rad)
  Support = -> [DatumPlane016]
  sketch-geometry (4):
    g0: LineSegment StartX=63 StartY=7.82e-14 StartZ=0 EndX=27.5 EndY=7.82e-14 EndZ=0
    g1: LineSegment StartX=27.5 StartY=7.82e-14 StartZ=0 EndX=27.5 EndY=-27.4148 EndZ=0
    g2: LineSegment StartX=27.5 StartY=-27.4148 StartZ=0 EndX=63 EndY=-27.4148 EndZ=0
    g3: LineSegment StartX=63 StartY=-27.4148 StartZ=0 EndX=63 EndY=7.82e-14 EndZ=0
  constraints (11):
    c: Coincident(g0,g1)
    c: Coincident(g2,g3)
    c: Coincident(g3,g0)
    c: Horizontal(g0)
    c: Horizontal(g2)
    c: Vertical(g1)
    c: Vertical(g3)
    c: Coincident(g0,g-3)
    c: DistanceY(g-4,g1) = 10
    c: Vertical(g1,g-5)
    c: Coincident(g2,g1)
FEATURE [PartDesign::Pocket] Pocket010
  BaseFeature = -> Pocket009
  Direction = (1,1e-16,-7e-16)
  Length = 5
  Length2 = 5
  Placement = pos=(7,1.55e-14,37.4148) rot=(0.707107,0.707107,0;3.14159rad)
  Profile = -> Sketch023
  ReferenceAxis = -> Sketch023 [N_Axis]
  Type = 1
FEATURE [PartDesign::Plane] DatumPlane017
  AttachmentOffset = pos=(0,0,0) rot=(1,0,0;3.14159rad)
  Length = 126.986
  MapMode = 5
  Placement = pos=(-51,1.55e-14,37.4148) rot=(0.57735,-0.57735,-0.57735;2.0944rad)
  ResizeMode = 0
  Support = -> [Pocket010]
  Width = 84.6204
FEATURE [Sketcher::SketchObject] Sketch024
  ExternalGeometry = -> [Sketch023]
  FullyConstrained = true
  MapMode = 5
  Placement = pos=(-51,1.55e-14,37.4148) rot=(-0.57735,0.57735,0.57735;4.18879rad)
  Support = -> [DatumPlane017]
  sketch-geometry (4):
    g0: LineSegment StartX=63 StartY=9.95e-14 StartZ=0 EndX=27.5 EndY=9.95e-14 EndZ=0
    g1: LineSegment StartX=27.5 StartY=9.95e-14 StartZ=0 EndX=27.5 EndY=-27.4148 EndZ=0
    g2: LineSegment StartX=27.5 StartY=-27.4148 StartZ=0 EndX=63 EndY=-27.4148 EndZ=0
    g3: LineSegment StartX=63 StartY=-27.4148 StartZ=0 EndX=63 EndY=9.95e-14 EndZ=0
  constraints (10):
    c: Coincident(g0,g1)
    c: Coincident(g1,g2)
    c: Coincident(g2,g3)
    c: Coincident(g3,g0)
    c: Horizontal(g0)
    c: Horizontal(g2)
    c: Vertical(g1)
    c: Vertical(g3)
    c: Coincident(g0,g-3)
    c: Coincident(g1,g-4)
FEATURE [PartDesign::Pocket] Pocket011
  BaseFeature = -> Pocket010
  Direction = (1,0,-1.1e-15)
  Length = 5
  Length2 = 5
  Placement = pos=(7,1.55e-14,37.4148) rot=(0.707107,0.707107,0;3.14159rad)
  Profile = -> Sketch024
  ReferenceAxis = -> Sketch024 [N_Axis]
  Reversed = true
  Type = 1
FEATURE [Part::FeaturePython] Screw005  label="M3x14-Screw001"  # Fasteners workbench fastener (typed FeaturePython)
  Placement = pos=(10,-75.7806,35.4148) rot=(0.72116,0.692769,0;3.14159rad)
  baseObject = -> Body006 [Edge98]
  diameter = 4
  invert = true
  leftHanded = false
  length = 5
  lengthCustom = 14
  matchOuter = false
  offset = 0
  thread = true
  type = 48
FEATURE [PartDesign::Plane] DatumPlane018
  Length = 132.926
  MapMode = 5
  Placement = pos=(7,-3.7e-15,42.4148) rot=(0,0,1;1.5708rad)
  ResizeMode = 0
  Support = -> [Pocket011]
  Width = 145.146
FEATURE [Sketcher::SketchObject] Sketch025
  ExternalGeometry = -> [Sketch019]
  FullyConstrained = true
  MapMode = 5
  Placement = pos=(7,-3.7e-15,42.4148) rot=(0,0,1;1.5708rad)
  Support = -> [DatumPlane018]
  expr: Constraints[1] = <<s>>.durchmesser_clips_loch
  sketch-geometry (14):
    g0: Circle CenterX=-27.5 CenterY=21.5 CenterZ=0 NormalX=0 NormalY=0 NormalZ=1 AngleXU=0 Radius=1
    g1: Circle CenterX=-27.5 CenterY=-21.5 CenterZ=0 NormalX=0 NormalY=0 NormalZ=1 AngleXU=0 Radius=1
    g2: Circle CenterX=-73.8903 CenterY=63 CenterZ=0 NormalX=0 NormalY=0 NormalZ=1 AngleXU=0 Radius=1
    g3: Circle CenterX=-73.8903 CenterY=-49 CenterZ=0 NormalX=0 NormalY=0 NormalZ=1 AngleXU=0 Radius=1
    g4: GeomPoint X=-63 Y=68 Z=0
    g5: Circle CenterX=-84.7806 CenterY=68 CenterZ=0 NormalX=0 NormalY=0 NormalZ=1 AngleXU=0 Radius=21.7806
    g6: Circle CenterX=-63 CenterY=68 CenterZ=0 NormalX=0 NormalY=0 NormalZ=1 AngleXU=0 Radius=21.7806
    g7: GeomPoint X=-73.8903 Y=49.1375 Z=0
    g8: Circle CenterX=-27.5 CenterY=68 CenterZ=0 NormalX=0 NormalY=0 NormalZ=1 AngleXU=0 Radius=10
    g9: Circle CenterX=-27.5 CenterY=58 CenterZ=0 NormalX=0 NormalY=0 NormalZ=1 AngleXU=0 Radius=10
    g10: GeomPoint X=-36.1603 Y=63 Z=0
    g11: Circle CenterX=-27.5 CenterY=-44 CenterZ=0 NormalX=0 NormalY=0 NormalZ=1 AngleXU=0 Radius=10
    g12: Circle CenterX=-27.5 CenterY=-54 CenterZ=0 NormalX=0 NormalY=0 NormalZ=1 AngleXU=0 Radius=10
    g13: GeomPoint X=-36.1603 Y=-49 Z=0
  constraints (30):
    c: Coincident(g0,g-6)
    c: Diameter(g0) = 2
    c: Coincident(g1,g-5)
    c: Equal(g1,g0)
    c: Equal(g2,g0)
    c: Equal(g3,g0)
    c: Horizontal(g4,g-3)
    c: Vertical(g4,g-4)
    c: Coincident(g5,g-3)
    c: PointOnObject(g4,g5)
    c: Coincident(g6,g4)
    c: PointOnObject(g5,g6)
    c: PointOnObject(g7,g5)
    c: PointOnObject(g7,g6)
    c: Vertical(g2,g7)
    c: Coincident(g8,g-7)
    c: PointOnObject(g-7,g8)
    c: Coincident(g9,g-7)
    c: PointOnObject(g8,g9)
    c: PointOnObject(g10,g8)
    c: PointOnObject(g10,g9)
    c: Horizontal(g10,g2)
    c: Vertical(g3,g2)
    c: Coincident(g11,g-8)
    c: PointOnObject(g-8,g11)
    c: Coincident(g12,g-8)
    c: PointOnObject(g11,g12)
    c: PointOnObject(g13,g11)
    c: PointOnObject(g13,g12)
    c: Horizontal(g13,g3)
FEATURE [PartDesign::Pocket] Pocket012  label="PocketWithClipsForCover"
  BaseFeature = -> Pocket011
  Direction = (-3.7e-15,3.9e-15,-1)
  Length = 5
  Length2 = 5
  Placement = pos=(7,1.55e-14,37.4148) rot=(0.707107,0.707107,0;3.14159rad)
  Profile = -> Sketch025
  ReferenceAxis = -> Sketch025 [N_Axis]
  Type = 1
FEATURE [PartDesign::Body] Body006  label="teil3"
  Group = -> [ShapeBinder007,DatumPlane013,Sketch017,DatumPlane014,Sketch018,AdditiveLoft001,ShapeBinder008,Sketch019,Pad008,Sketch020,Pocket007,Sketch021,Pocket008,DatumPlane015,Sketch022,Pocket009,DatumPlane016,Sketch023,Pocket010,DatumPlane017,Sketch024,Pocket011,DatumPlane018,Sketch025,Pocket012]
  Origin = -> Origin006
  Tip = -> Pocket012
FEATURE [PartDesign::ShapeBinder] ShapeBinder  label="ShapeBinderTeil"
  Placement = pos=(7,1.55e-14,37.4148) rot=(0.707107,0.707107,0;3.14159rad)
  TraceSupport = false
FEATURE [PartDesign::ShapeBinder] ShapeBinder009  label="ShapeBinderWaegeZelle"
  Support = -> [Body005]
  TraceSupport = false
FEATURE [PartDesign::ShapeBinder] ShapeBinder010  label="ShapeBinderBasePlateWaage"
  Support = -> [Body004]
  TraceSupport = false
FEATURE [PartDesign::Plane] DatumPlane020  label="DatumPlaneRechteSeiteTeil"
  AttachmentOffset = pos=(0,0,5) rot=(0,0,1;3.14159rad)
  Length = 61.1727
  MapMode = 5
  Placement = pos=(7,-89.7806,37.4148) rot=(1,0,0;1.5708rad)
  ResizeMode = 0
  Support = -> [ShapeBinder]
  Width = 73.5875
  expr: .AttachmentOffset.Base.z = <<s>>.x_ueberstand_cover
FEATURE [Sketcher::SketchObject] Sketch027  label="SketchFront"
  ExternalGeometry = -> [ShapeBinder010,ShapeBinder]
  FullyConstrained = true
  MapMode = 5
  Placement = pos=(7,-89.7806,37.4148) rot=(1,0,0;1.5708rad)
  Support = -> [DatumPlane020]
  expr: Constraints[13] = <<s>>.dicke_cover
  expr: Constraints[14] = <<s>>.dicke_cover
  expr: Constraints[16] = <<s>>.y_abstand_cover_zu_vorderseite_teil
  expr: Constraints[17] = <<s>>.z_hoehe_ueber_base_plate
  sketch-geometry (11):
    g0: LineSegment StartX=-21.5 StartY=26 StartZ=0 EndX=-83.5674 EndY=26 EndZ=0
    g1: LineSegment StartX=-104.781 StartY=4.7868 StartZ=0 EndX=-104.781 EndY=-37.4148 EndZ=0
    g2: LineSegment StartX=-104.781 StartY=-37.4148 StartZ=0 EndX=-107.781 EndY=-37.4148 EndZ=0
    g3: LineSegment StartX=-107.781 StartY=-37.4148 StartZ=0 EndX=-107.781 EndY=7.7868 EndZ=0
    g4: LineSegment StartX=-107.781 StartY=7.7868 StartZ=0 EndX=-86.5674 EndY=29 EndZ=0
    g5: LineSegment StartX=-86.5674 StartY=29 StartZ=0 EndX=-21.5 EndY=29 EndZ=0
    g6: LineSegment StartX=-21.5 StartY=29 StartZ=0 EndX=-21.5 EndY=26 EndZ=0
    g7: LineSegment StartX=-104.781 StartY=4.7868 StartZ=0 EndX=-107.781 EndY=7.7868 EndZ=0
    g8: LineSegment StartX=-83.5674 StartY=26 StartZ=0 EndX=-86.5674 EndY=29 EndZ=0
    g9: LineSegment StartX=-104.781 StartY=4.7868 StartZ=0 EndX=-83.5674 EndY=4.7868 EndZ=0
    g10: LineSegment StartX=-83.5674 StartY=26 StartZ=0 EndX=-83.5674 EndY=4.7868 EndZ=0
  constraints (31):
    c: Horizontal(g0)
    c: Vertical(g1)
    c: Coincident(g1,g2)
    c: Horizontal(g2)
    c: Coincident(g2,g3)
    c: Vertical(g3)
    c: Coincident(g3,g4)
    c: Coincident(g4,g5)
    c: Horizontal(g5)
    c: Coincident(g5,g6)
    c: Coincident(g6,g0)
    c: Vertical(g6)
    c: Horizontal(g1,g-6)
    c: DistanceY(g6,g6) = 3
    c: DistanceX(g2,g1) = 3
    c: Vertical(g0,g-5)
    c: DistanceX(g1,g-6) = 20
    c: DistanceY(g-3,g0) = 10
    c: Coincident(g8,g0)
    c: Coincident(g8,g4)
    c: Coincident(g7,g3)
    c: Parallel(g8,g7)
    c: Distance(g4) = 30
    c: Angle(g7,g4) = 1.5708
    c: Angle(g4,g5) = 2.35619
    c: Coincident(g9,g1)
    c: Horizontal(g9)
    c: Coincident(g10,g0)
    c: Coincident(g10,g9)
    c: Vertical(g10)
    c: Coincident(g1,g7)
FEATURE [PartDesign::Pad] Pad009
  Direction = (1,0,-1.8e-15)
  Length = 132
  Length2 = 10
  Placement = pos=(66,1.5e-14,37.4148) rot=(0.57735,0.57735,0.57735;2.0944rad)
  Profile = -> Sketch027
  ReferenceAxis = -> Sketch027 [N_Axis]
  Reversed = true
  Type = 0
  expr: Length = <<s>>.x_pad_cover
FEATURE [Sketcher::SketchObject] Sketch028  label="SketchAbschlussRechts"
  ExternalGeometry = -> [Sketch027]
  FullyConstrained = true
  MapMode = 5
  Placement = pos=(66,1.5e-14,37.4148) rot=(0.57735,0.57735,0.57735;2.0944rad)
  Support = -> [DatumPlane020]
  sketch-geometry (5):
    g0: LineSegment StartX=-21.5 StartY=29 StartZ=0 EndX=-86.5674 EndY=29 EndZ=0
    g1: LineSegment StartX=-86.5674 StartY=29 StartZ=0 EndX=-107.781 EndY=7.7868 EndZ=0
    g2: LineSegment StartX=-107.781 StartY=7.7868 StartZ=0 EndX=-107.781 EndY=-37.4148 EndZ=0
    g3: LineSegment StartX=-107.781 StartY=-37.4148 StartZ=0 EndX=-21.5 EndY=-37.4148 EndZ=0
    g4: LineSegment StartX=-21.5 StartY=-37.4148 StartZ=0 EndX=-21.5 EndY=29 EndZ=0
  constraints (11):
    c: Coincident(g-3,g0)
    c: Coincident(g0,g-3)
    c: Coincident(g0,g1)
    c: Coincident(g1,g-4)
    c: Coincident(g1,g2)
    c: Coincident(g2,g-4)
    c: Coincident(g2,g3)
    c: Horizontal(g3)
    c: Coincident(g3,g4)
    c: Coincident(g4,g0)
    c: Vertical(g4)
FEATURE [PartDesign::Pad] Pad010
  BaseFeature = -> Pad009
  Direction = (1,0,-1.8e-15)
  Length = 3
  Length2 = 10
  Placement = pos=(66,1.5e-14,37.4148) rot=(0.57735,0.57735,0.57735;2.0944rad)
  Profile = -> Sketch028
  ReferenceAxis = -> Sketch028 [N_Axis]
  Type = 0
  expr: Length = <<s>>.dicke_cover
FEATURE [PartDesign::Plane] DatumPlane021  label="DatumPlaneLinkeSeiteAbschluss"
  Length = 61.1727
  MapMode = 5
  Placement = pos=(-66,6.9e-14,37.4148) rot=(-0.57735,-0.57735,0.57735;2.0944rad)
  ResizeMode = 0
  Support = -> [Pad010]
  Width = 73.5875
FEATURE [Sketcher::SketchObject] Sketch029  label="SketchAbschlussLinks"
  ExternalGeometry = -> [Pad010]
  FullyConstrained = true
  MapMode = 5
  Placement = pos=(-66,6.9e-14,37.4148) rot=(-0.57735,-0.57735,0.57735;2.0944rad)
  Support = -> [DatumPlane021]
  sketch-geometry (5):
    g0: LineSegment StartX=-107.781 StartY=37.4148 StartZ=0 EndX=-107.781 EndY=-7.7868 EndZ=0
    g1: LineSegment StartX=-107.781 StartY=-7.7868 StartZ=0 EndX=-86.5674 EndY=-29 EndZ=0
    g2: LineSegment StartX=-86.5674 StartY=-29 StartZ=0 EndX=-21.5 EndY=-29 EndZ=0
    g3: LineSegment StartX=-21.5 StartY=-29 StartZ=0 EndX=-21.5 EndY=37.4148 EndZ=0
    g4: LineSegment StartX=-21.5 StartY=37.4148 StartZ=0 EndX=-107.781 EndY=37.4148 EndZ=0
  constraints (11):
    c: Coincident(g-4,g0)
    c: Coincident(g0,g-4)
    c: Coincident(g0,g1)
    c: Coincident(g1,g-3)
    c: Coincident(g1,g2)
    c: Coincident(g2,g-3)
    c: Coincident(g2,g3)
    c: Vertical(g3)
    c: Coincident(g3,g4)
    c: Coincident(g4,g0)
    c: Horizontal(g4)
FEATURE [PartDesign::Pad] Pad011
  BaseFeature = -> Pad010
  Direction = (-1,4e-16,1.8e-15)
  Length = 3
  Length2 = 10
  Placement = pos=(66,1.5e-14,37.4148) rot=(0.57735,0.57735,0.57735;2.0944rad)
  Profile = -> Sketch029
  ReferenceAxis = -> Sketch029 [N_Axis]
  Type = 0
  expr: Length = <<s>>.dicke_cover
FEATURE [PartDesign::Plane] DatumPlane022
  Length = 63.4907
  MapMode = 5
  Placement = pos=(66,-2.85e-14,66.4148) rot=(0,0,-1;1.5708rad)
  ResizeMode = 0
  Support = -> [Pad011]
  Width = 104.491
FEATURE [Sketcher::SketchObject] Sketch030
  ExternalGeometry = -> [ShapeBinder010]
  FullyConstrained = true
  MapMode = 5
  Placement = pos=(66,-2.85e-14,66.4148) rot=(0,0,-1;1.5708rad)
  Support = -> [DatumPlane022]
  expr: Constraints[1] = <<s>>.dose_durchmesser
  sketch-geometry (1):
    g0: Circle CenterX=56.2806 CenterY=-59 CenterZ=0 NormalX=0 NormalY=0 NormalZ=1 AngleXU=0 Radius=29
  constraints (2):
    c: Coincident(g0,g-3)
    c: Diameter(g0) = 58
FEATURE [Mesh::Feature] Mesh004  label="PocketWithClipsForCoverAndCutoutsForM3Nuts (Meshed)"
FEATURE [PartDesign::ShapeBinder] ShapeBinder011  label="ShapeBinderCover"
  Placement = pos=(66,1.5e-14,37.4148) rot=(0.57735,0.57735,0.57735;2.0944rad)
  Support = -> [Pad009]
  TraceSupport = false
FEATURE [PartDesign::Plane] DatumPlane025
  Length = 86.754
  MapMode = 5
  Placement = pos=(66,-57.7837,95.1984) rot=(0.357407,0.357407,-0.862856;1.71777rad)
  ResizeMode = 0
  Support = -> [ShapeBinder011]
  Width = 107.043
FEATURE [Sketcher::SketchObject] Sketch034  label="SketchDisplayFront"
  ExternalGeometry = -> [ShapeBinder011]
  FullyConstrained = true
  MapMode = 5
  Placement = pos=(66,-57.7837,95.1984) rot=(0.357407,0.357407,-0.862856;1.71777rad)
  Support = -> [DatumPlane025]
  expr: Constraints[11] = <<s>>.display_hoehe
  expr: Constraints[12] = <<s>>.display_breite
  sketch-geometry (9):
    g0: LineSegment StartX=40.7063 StartY=-1.42e-14 StartZ=0 EndX=70.7063 EndY=-132 EndZ=0
    g1: LineSegment StartX=40.7063 StartY=-132 StartZ=0 EndX=70.7063 EndY=-2.84e-14 EndZ=0
    g2: GeomPoint X=55.7063 Y=-66 Z=0
    g3: GeomPoint X=55.7063 Y=-66 Z=0
    g4: LineSegment StartX=48.7063 StartY=-83 StartZ=0 EndX=48.7063 EndY=-112 EndZ=0
    g5: LineSegment StartX=48.7063 StartY=-112 StartZ=0 EndX=62.7063 EndY=-112 EndZ=0
    g6: LineSegment StartX=62.7063 StartY=-112 StartZ=0 EndX=62.7063 EndY=-83 EndZ=0
    g7: LineSegment StartX=62.7063 StartY=-83 StartZ=0 EndX=48.7063 EndY=-83 EndZ=0
    g8: GeomPoint X=55.7063 Y=-97.5 Z=0
  constraints (20):
    c: Coincident(g3,g2)
    c: PointOnObject(g2,g0)
    c: Coincident(g4,g5)
    c: Coincident(g5,g6)
    c: Coincident(g6,g7)
    c: Coincident(g7,g4)
    c: Horizontal(g5)
    c: Horizontal(g7)
    c: Vertical(g4)
    c: Vertical(g6)
    c: Symmetric(g5,g4,g8)
    c: DistanceX(g7,g7) = 14
    c: DistanceY(g4,g4) = 29
    c: Vertical(g2,g8)
    c: DistanceY(g0,g4) = 20
    c: Coincident(g1,g-3)
    c: Coincident(g0,g-3)
    c: Coincident(g0,g-4)
    c: Coincident(g1,g-4)
    c: PointOnObject(g2,g1)
FEATURE [PartDesign::Pad] Pad014  label="PadDisplay"
  Direction = (1.1e-15,-0.707107,0.707107)
  Length = 2
  Length2 = 10
  Placement = pos=(66,-57.7837,95.1984) rot=(0.357407,0.357407,-0.862856;1.71777rad)
  Profile = -> Sketch034
  ReferenceAxis = -> Sketch034 [N_Axis]
  Reversed = true
  Type = 0
  expr: Length = <<s>>.display_extrusion
FEATURE [PartDesign::Plane] DatumPlane026
  Length = 86.754
  MapMode = 5
  Placement = pos=(66,-56.3695,93.7842) rot=(-0.678598,0.678598,0.281085;2.59356rad)
  ResizeMode = 0
  Support = -> [Pad014]
  Width = 107.043
FEATURE [Sketcher::SketchObject] Sketch035  label="SketchPCB"
  ExternalGeometry = -> [Pad014]
  FullyConstrained = true
  MapMode = 5
  Placement = pos=(66,-56.3695,93.7842) rot=(-0.678598,0.678598,0.281085;2.59356rad)
  Support = -> [DatumPlane026]
  expr: Constraints[16] = <<s>>.display_pcb_hoehe
  expr: Constraints[17] = <<s>>.display_pcb_breite
  sketch-geometry (8):
    g0: LineSegment StartX=48.7063 StartY=112 StartZ=0 EndX=62.7063 EndY=83 EndZ=0
    g1: LineSegment StartX=48.7063 StartY=83 StartZ=0 EndX=62.7063 EndY=112 EndZ=0
    g2: GeomPoint X=55.7063 Y=97.5 Z=0
    g3: LineSegment StartX=43.2063 StartY=113 StartZ=0 EndX=43.2063 EndY=82 EndZ=0
    g4: LineSegment StartX=43.2063 StartY=82 StartZ=0 EndX=68.2063 EndY=82 EndZ=0
    g5: LineSegment StartX=68.2063 StartY=82 StartZ=0 EndX=68.2063 EndY=113 EndZ=0
    g6: LineSegment StartX=68.2063 StartY=113 StartZ=0 EndX=43.2063 EndY=113 EndZ=0
    g7: GeomPoint X=55.7063 Y=97.5 Z=0
  constraints (18):
    c: Coincident(g0,g-3)
    c: Coincident(g0,g-4)
    c: Coincident(g1,g-4)
    c: Coincident(g1,g-3)
    c: PointOnObject(g2,g0)
    c: PointOnObject(g2,g1)
    c: Coincident(g3,g4)
    c: Coincident(g4,g5)
    c: Coincident(g5,g6)
    c: Coincident(g6,g3)
    c: Horizontal(g4)
    c: Horizontal(g6)
    c: Vertical(g3)
    c: Vertical(g5)
    c: Symmetric(g4,g3,g7)
    c: Coincident(g7,g2)
    c: DistanceX(g6,g6) = 25
    c: DistanceY(g5,g5) = 31
FEATURE [PartDesign::Pad] Pad015  label="PadPCB"
  BaseFeature = -> Pad014
  Direction = (-1.2e-15,0.707107,-0.707107)
  Length = 5
  Length2 = 10
  Placement = pos=(66,-57.7837,95.1984) rot=(0.357407,0.357407,-0.862856;1.71777rad)
  Profile = -> Sketch035
  ReferenceAxis = -> Sketch035 [N_Axis]
  Type = 0
  expr: Length = <<s>>.display_pcb_extrusion
FEATURE [PartDesign::Body] Body009  label="Display"
  Group = -> [ShapeBinder011,DatumPlane025,Sketch034,Pad014,DatumPlane026,Sketch035,Pad015]
  Origin = -> Origin009
  Tip = -> Pad015
FEATURE [PartDesign::ShapeBinder] ShapeBinder012  label="ShapeBinderCover001"
  Placement = pos=(66,1.5e-14,37.4148) rot=(0.57735,0.57735,0.57735;2.0944rad)
  Support = -> [Pad009]
  TraceSupport = false
FEATURE [PartDesign::Plane] DatumPlane027
  AttachmentOffset = pos=(0,0,1) rot=(0,0,1;0rad)
  Length = 187.462
  MapMode = 5
  Placement = pos=(66,-58.4908,95.9055) rot=(0.357407,0.357407,-0.862856;1.71777rad)
  ResizeMode = 0
  Support = -> [ShapeBinder012]
  Width = 160.932
  expr: .AttachmentOffset.Base.z = <<s>>.button_kappe_ueberstand
FEATURE [Sketcher::SketchObject] Sketch036  label="SketchKappe"
  ExternalGeometry = -> [ShapeBinder012]
  FullyConstrained = true
  MapMode = 5
  Placement = pos=(66,-58.4908,95.9055) rot=(0.357407,0.357407,-0.862856;1.71777rad)
  Support = -> [DatumPlane027]
  expr: Constraints[15] = <<s>>.ende_display_von_links
  expr: Constraints[3] = <<s>>.button_kappe_durchmesser
  expr: Constraints[4] = <<s>>.button_abstand / 2
  sketch-geometry (7):
    g0: GeomPoint X=55.7063 Y=-41.5 Z=0
    g1: Circle CenterX=55.7063 CenterY=-29.6 CenterZ=0 NormalX=0 NormalY=0 NormalZ=1 AngleXU=0 Radius=6.9
    g2: GeomPoint X=55.7063 Y=-36.5 Z=0
    g3: GeomPoint X=55.7063 Y=-41.5 Z=0
    g4: LineSegment StartX=40.7063 StartY=-83 StartZ=0 EndX=70.7063 EndY=-83 EndZ=0
    g5: LineSegment StartX=40.7063 StartY=1.42e-14 StartZ=0 EndX=70.7063 EndY=-83 EndZ=0
    g6: LineSegment StartX=40.7063 StartY=-83 StartZ=0 EndX=70.7063 EndY=-1.42e-14 EndZ=0
  constraints (16):
    c: Vertical(g1,g0)
    c: PointOnObject(g2,g1)
    c: Vertical(g2,g1)
    c: Diameter(g1) = 13.8
    c: DistanceY(g0,g2) = 5
    c: Horizontal(g4)
    c: Coincident(g5,g4)
    c: Coincident(g6,g4)
    c: PointOnObject(g3,g5)
    c: PointOnObject(g3,g6)
    c: Coincident(g0,g3)
    c: Coincident(g6,g-3)
    c: Coincident(g5,g-3)
    c: Vertical(g4,g-4)
    c: Vertical(g4,g-4)
    c: DistanceY(g-4,g4) = 49
FEATURE [PartDesign::Pad] Pad016  label="PadKappe"
  Direction = (1.1e-15,-0.707107,0.707107)
  Length = 4
  Length2 = 10
  Placement = pos=(66,-58.4908,95.9055) rot=(0.357407,0.357407,-0.862856;1.71777rad)
  Profile = -> Sketch036
  ReferenceAxis = -> Sketch036 [N_Axis]
  Reversed = true
  Type = 0
  expr: Length = <<s>>.button_kappe_hoehe
FEATURE [PartDesign::Plane] DatumPlane028
  Length = 187.462
  MapMode = 5
  Placement = pos=(66,-55.6624,93.0771) rot=(-0.678598,0.678598,0.281085;2.59356rad)
  ResizeMode = 0
  Support = -> [Pad016]
  Width = 160.932
FEATURE [Sketcher::SketchObject] Sketch037  label="SketchKappeGross"
  ExternalGeometry = -> [Sketch036]
  FullyConstrained = true
  MapMode = 5
  Placement = pos=(66,-55.6624,93.0771) rot=(0.678598,-0.678598,-0.281085;3.68962rad)
  Support = -> [DatumPlane028]
  expr: Constraints[1] = <<s>>.button_kappe_durchmesser_gross
  sketch-geometry (1):
    g0: Circle CenterX=55.7063 CenterY=29.6 CenterZ=0 NormalX=0 NormalY=0 NormalZ=1 AngleXU=0 Radius=7
  constraints (2):
    c: Coincident(g0,g-3)
    c: Diameter(g0) = 14
FEATURE [PartDesign::Pad] Pad017  label="PadKappeGrossLippe"
  BaseFeature = -> Pad016
  Direction = (-1.4e-15,0.707107,-0.707107)
  Length = 4.5
  Length2 = 10
  Placement = pos=(66,-58.4908,95.9055) rot=(0.357407,0.357407,-0.862856;1.71777rad)
  Profile = -> Sketch037
  ReferenceAxis = -> Sketch037 [N_Axis]
  Type = 0
  expr: Length = <<s>>.button_kappe_gross_hoehe
FEATURE [Sketcher::SketchObject] Sketch038
  FullyConstrained = true
  MapMode = 5
  Placement = pos=(66,-52.4804,89.8951) rot=(-0.678598,0.678598,0.281085;2.59356rad)
  Support = -> [Pad017]
FEATURE [PartDesign::Plane] DatumPlane029
  Length = 187.462
  MapMode = 5
  Placement = pos=(66,-52.4804,89.8951) rot=(-0.678598,0.678598,0.281085;2.59356rad)
  ResizeMode = 0
  Support = -> [Pad017]
  Width = 160.932
FEATURE [Sketcher::SketchObject] Sketch039  label="SketchBase"
  ExternalGeometry = -> [Pad017]
  FullyConstrained = true
  MapMode = 5
  Placement = pos=(66,-52.4804,89.8951) rot=(-0.678598,0.678598,0.281085;2.59356rad)
  Support = -> [DatumPlane029]
  expr: Constraints[11] = <<s>>.button_base_seitenlaenge
  sketch-geometry (5):
    g0: LineSegment StartX=49.2063 StartY=23.1 StartZ=0 EndX=49.2063 EndY=36.1 EndZ=0
    g1: LineSegment StartX=49.2063 StartY=36.1 StartZ=0 EndX=62.2063 EndY=36.1 EndZ=0
    g2: LineSegment StartX=62.2063 StartY=36.1 StartZ=0 EndX=62.2063 EndY=23.1 EndZ=0
    g3: LineSegment StartX=62.2063 StartY=23.1 StartZ=0 EndX=49.2063 EndY=23.1 EndZ=0
    g4: GeomPoint X=55.7063 Y=29.6 Z=0
  constraints (12):
    c: Coincident(g0,g1)
    c: Coincident(g1,g2)
    c: Coincident(g2,g3)
    c: Coincident(g3,g0)
    c: Horizontal(g1)
    c: Horizontal(g3)
    c: Vertical(g0)
    c: Vertical(g2)
    c: Symmetric(g1,g0,g4)
    c: Coincident(g4,g-3)
    c: Equal(g2,g3)
    c: DistanceX(g3,g3) = 13
FEATURE [PartDesign::Pad] Pad018  label="PadButtonWithBase"
  BaseFeature = -> Pad017
  Direction = (-1.3e-15,0.707107,-0.707107)
  Length = 15
  Length2 = 10
  Placement = pos=(66,-58.4908,95.9055) rot=(0.357407,0.357407,-0.862856;1.71777rad)
  Profile = -> Sketch039
  ReferenceAxis = -> Sketch039 [N_Axis]
  Type = 0
  expr: Length = <<s>>.button_base_extrusion
FEATURE [PartDesign::Body] Body008  label="Button1"
  Group = -> [ShapeBinder012,DatumPlane027,Sketch036,Pad016,DatumPlane028,Sketch037,Pad017,Sketch038,DatumPlane029,Sketch039,Pad018]
  Origin = -> Origin008
  Tip = -> Pad018
FEATURE [PartDesign::Plane] DatumPlane030
  AttachmentOffset = pos=(0,0,0) rot=(1,0,0;1.5708rad)
  Length = 61.6116
  MapMode = 5
  Placement = pos=(7,-5.8e-15,42.4148) rot=(0.57735,0.57735,0.57735;2.0944rad)
  ResizeMode = 0
  Support = -> [ShapeBinder]
  Width = 79.0264
FEATURE [Sketcher::SketchObject] Sketch040  label="SketchCutoutMitte"
  ExternalGeometry = -> [Sketch027]
  FullyConstrained = true
  MapMode = 5
  Placement = pos=(7,-5.8e-15,42.4148) rot=(0.57735,0.57735,0.57735;2.0944rad)
  Support = -> [DatumPlane030]
  sketch-geometry (3):
    g0: LineSegment StartX=-104.781 StartY=-0.213203 StartZ=0 EndX=-83.5674 EndY=-0.213203 EndZ=0
    g1: LineSegment StartX=-83.5674 StartY=-0.213203 StartZ=0 EndX=-83.5674 EndY=21 EndZ=0
    g2: LineSegment StartX=-83.5674 StartY=21 StartZ=0 EndX=-104.781 EndY=-0.213203 EndZ=0
  constraints (6):
    c: Coincident(g-4,g0)
    c: Coincident(g0,g-4)
    c: Coincident(g0,g1)
    c: Coincident(g1,g-3)
    c: Coincident(g1,g2)
    c: Coincident(g2,g0)
FEATURE [PartDesign::Pocket] Pocket016  label="PocketCutoutMitte"
  BaseFeature = -> Pad011
  Direction = (-1,2e-16,4e-15)
  Length = 40
  Length2 = 5
  Midplane = true
  Placement = pos=(66,1.5e-14,37.4148) rot=(0.57735,0.57735,0.57735;2.0944rad)
  Profile = -> Sketch040
  ReferenceAxis = -> Sketch040 [N_Axis]
  Type = 0
FEATURE [PartDesign::Pocket] Pocket014  label="PocketFuerDose"
  BaseFeature = -> Pocket016
  Direction = (-1.4e-15,1.5e-15,-1)
  Length = 5
  Length2 = 5
  Placement = pos=(66,1.5e-14,37.4148) rot=(0.57735,0.57735,0.57735;2.0944rad)
  Profile = -> Sketch030
  ReferenceAxis = -> Sketch030 [N_Axis]
  Type = 1
FEATURE [PartDesign::Plane] DatumPlane023  label="DatumPlaneUnterseiteCover"
  Length = 63.4907
  MapMode = 5
  Placement = pos=(66,-1.53e-14,63.4148) rot=(0.707107,0.707107,0;3.14159rad)
  ResizeMode = 0
  Support = -> [Pocket014]
  Width = 104.491
FEATURE [Sketcher::SketchObject] Sketch031
  ExternalGeometry = -> [Pocket014,Sketch030]
  FullyConstrained = true
  MapMode = 5
  Placement = pos=(66,-1.53e-14,63.4148) rot=(0.707107,0.707107,0;3.14159rad)
  Support = -> [DatumPlane023]
  expr: Constraints[1] = <<s>>.dose_verstaerkung_breite
  sketch-geometry (3):
    g0: Circle CenterX=-56.2806 CenterY=-59 CenterZ=0 NormalX=0 NormalY=0 NormalZ=1 AngleXU=0 Radius=29
    g1: LineSegment StartX=-86.7806 StartY=-59 StartZ=0 EndX=-85.2806 EndY=-59 EndZ=0
    g2: Circle CenterX=-56.2806 CenterY=-59 CenterZ=0 NormalX=0 NormalY=0 NormalZ=1 AngleXU=0 Radius=30.5
  constraints (8):
    c: Horizontal(g1)
    c: Distance(g1) = 1.5
    c: Horizontal(g1,g0)
    c: Coincident(g2,g0)
    c: PointOnObject(g1,g2)
    c: PointOnObject(g1,g0)
    c: Coincident(g0,g-4)
    c: PointOnObject(g1,g-4)
FEATURE [PartDesign::Pad] Pad012  label="PadVerstaerkungPocket"
  BaseFeature = -> Pocket014
  Direction = (-1.1e-15,1.2e-15,-1)
  Length = 5
  Length2 = 10
  Placement = pos=(66,1.5e-14,37.4148) rot=(0.57735,0.57735,0.57735;2.0944rad)
  Profile = -> Sketch031
  ReferenceAxis = -> Sketch031 [N_Axis]
  Type = 3
  UpToFace = -> ShapeBinder [Face34]
  expr: Length = <<s>>.dose_verstaerkung_pad
FEATURE [Sketcher::SketchObject] Sketch032  label="SketchPillars"
  ExternalGeometry = -> [ShapeBinder]
  FullyConstrained = true
  MapMode = 5
  Placement = pos=(66,-1.53e-14,63.4148) rot=(0.707107,0.707107,0;3.14159rad)
  Support = -> [DatumPlane023]
  expr: Constraints[7] = <<s>>.durchmesser_pillars
  sketch-geometry (4):
    g0: Circle CenterX=-73.8903 CenterY=-10 CenterZ=0 NormalX=0 NormalY=0 NormalZ=1 AngleXU=0 Radius=3.5
    g1: Circle CenterX=-27.5 CenterY=-37.5 CenterZ=0 NormalX=0 NormalY=0 NormalZ=1 AngleXU=0 Radius=3.5
    g2: Circle CenterX=-27.5 CenterY=-80.5 CenterZ=0 NormalX=0 NormalY=0 NormalZ=1 AngleXU=0 Radius=3.5
    g3: Circle CenterX=-73.8903 CenterY=-122 CenterZ=0 NormalX=0 NormalY=0 NormalZ=1 AngleXU=0 Radius=3.5
  constraints (8):
    c: Coincident(g0,g-3)
    c: Coincident(g1,g-4)
    c: Coincident(g2,g-5)
    c: Coincident(g3,g-6)
    c: Equal(g1,g0)
    c: Equal(g0,g2)
    c: Equal(g0,g3)
    c: Diameter(g0) = 7
FEATURE [PartDesign::Pad] Pad013  label="PadPillars"
  BaseFeature = -> Pad012
  Direction = (-1.1e-15,1.2e-15,-1)
  Length = 10
  Length2 = 10
  Placement = pos=(66,1.5e-14,37.4148) rot=(0.57735,0.57735,0.57735;2.0944rad)
  Profile = -> Sketch032
  ReferenceAxis = -> Sketch032 [N_Axis]
  Type = 3
  UpToFace = -> ShapeBinder [Face34]
FEATURE [PartDesign::Plane] DatumPlane024
  Length = 63.4907
  MapMode = 5
  Placement = pos=(66,1.5e-14,37.4148) rot=(0.707107,0.707107,0;3.14159rad)
  ResizeMode = 0
  Support = -> [Pad013]
  Width = 104.491
FEATURE [Sketcher::SketchObject] Sketch033  label="SketchPocketThreadedInserts"
  ExternalGeometry = -> [Sketch032]
  FullyConstrained = true
  MapMode = 5
  Placement = pos=(66,1.5e-14,37.4148) rot=(0.707107,0.707107,0;3.14159rad)
  Support = -> [DatumPlane024]
  expr: Constraints[7] = <<s>>.durchmesser_loch_threaded_inserts
  sketch-geometry (4):
    g0: Circle CenterX=-73.8903 CenterY=-10 CenterZ=0 NormalX=0 NormalY=0 NormalZ=1 AngleXU=0 Radius=0.9
    g1: Circle CenterX=-27.5 CenterY=-37.5 CenterZ=0 NormalX=0 NormalY=0 NormalZ=1 AngleXU=0 Radius=0.9
    g2: Circle CenterX=-27.5 CenterY=-80.5 CenterZ=0 NormalX=0 NormalY=0 NormalZ=1 AngleXU=0 Radius=0.9
    g3: Circle CenterX=-73.8903 CenterY=-122 CenterZ=0 NormalX=0 NormalY=0 NormalZ=1 AngleXU=0 Radius=0.9
  constraints (8):
    c: Coincident(g0,g-3)
    c: Coincident(g1,g-4)
    c: Coincident(g2,g-5)
    c: Coincident(g3,g-6)
    c: Equal(g3,g2)
    c: Equal(g3,g1)
    c: Equal(g3,g0)
    c: Diameter(g0) = 1.8
FEATURE [PartDesign::Pocket] Pocket015  label="PocketThreadedInserts001"
  BaseFeature = -> Pad013
  Direction = (3.7e-15,-3.8e-15,1)
  Length = 6.5
  Length2 = 5
  Placement = pos=(66,1.5e-14,37.4148) rot=(0.57735,0.57735,0.57735;2.0944rad)
  Profile = -> Sketch033
  ReferenceAxis = -> Sketch033 [N_Axis]
  Type = 0
  expr: Length = <<s>>.pocket_depth_threaded_inserts
FEATURE [PartDesign::Pocket] Pocket017  label="PocketCleanupUnderside"
  BaseFeature = -> Pocket015
  Direction = (-1,2e-16,3.2e-15)
  Length = 53
  Length2 = 5
  Placement = pos=(66,1.5e-14,37.4148) rot=(0.57735,0.57735,0.57735;2.0944rad)
  Profile = -> Pocket015 [Face10]
  Type = 0
FEATURE [PartDesign::ShapeBinder] ShapeBinder013  label="ShapeBinderCover002"
  Placement = pos=(66,1.5e-14,37.4148) rot=(0.57735,0.57735,0.57735;2.0944rad)
  Support = -> [Pad009]
  TraceSupport = false
FEATURE [PartDesign::Plane] DatumPlane031
  AttachmentOffset = pos=(0,0,1) rot=(0,0,1;0rad)
  Length = 86.754
  MapMode = 5
  Placement = pos=(66,-58.4908,95.9055) rot=(0.357407,0.357407,-0.862856;1.71777rad)
  ResizeMode = 0
  Support = -> [ShapeBinder013]
  Width = 107.043
  expr: .AttachmentOffset.Base.z = <<s>>.button_kappe_ueberstand
FEATURE [Sketcher::SketchObject] Sketch041  label="SketchKappe001"
  ExternalGeometry = -> [ShapeBinder013]
  FullyConstrained = true
  MapMode = 5
  Placement = pos=(66,-58.4908,95.9055) rot=(0.357407,0.357407,-0.862856;1.71777rad)
  Support = -> [DatumPlane031]
  expr: Constraints[15] = <<s>>.ende_display_von_links
  expr: Constraints[3] = <<s>>.button_kappe_durchmesser
  expr: Constraints[4] = <<s>>.button_abstand * 2.5
  sketch-geometry (7):
    g0: GeomPoint X=55.7063 Y=-41.5 Z=0
    g1: Circle CenterX=55.7063 CenterY=-9.6 CenterZ=0 NormalX=0 NormalY=0 NormalZ=1 AngleXU=0 Radius=6.9
    g2: GeomPoint X=55.7063 Y=-16.5 Z=0
    g3: GeomPoint X=55.7063 Y=-41.5 Z=0
    g4: LineSegment StartX=40.7063 StartY=-83 StartZ=0 EndX=70.7063 EndY=-83 EndZ=0
    g5: LineSegment StartX=40.7063 StartY=1.42e-14 StartZ=0 EndX=70.7063 EndY=-83 EndZ=0
    g6: LineSegment StartX=40.7063 StartY=-83 StartZ=0 EndX=70.7063 EndY=-1.42e-14 EndZ=0
  constraints (16):
    c: Vertical(g1,g0)
    c: PointOnObject(g2,g1)
    c: Vertical(g2,g1)
    c: Diameter(g1) = 13.8
    c: DistanceY(g0,g2) = 25
    c: Horizontal(g4)
    c: Coincident(g5,g4)
    c: Coincident(g6,g4)
    c: PointOnObject(g3,g5)
    c: PointOnObject(g3,g6)
    c: Coincident(g0,g3)
    c: Vertical(g6,g4)
    c: Vertical(g4,g5)
    c: Coincident(g6,g-3)
    c: Coincident(g5,g-3)
    c: DistanceY(g-4,g4) = 49
FEATURE [PartDesign::Pad] Pad019  label="PadKappe001"
  Direction = (1.1e-15,-0.707107,0.707107)
  Length = 4
  Length2 = 10
  Placement = pos=(66,-58.4908,95.9055) rot=(0.357407,0.357407,-0.862856;1.71777rad)
  Profile = -> Sketch041
  ReferenceAxis = -> Sketch041 [N_Axis]
  Reversed = true
  Type = 0
  expr: Length = <<s>>.button_kappe_hoehe
FEATURE [PartDesign::Plane] DatumPlane032
  Length = 86.754
  MapMode = 5
  Placement = pos=(66,-55.6624,93.0771) rot=(-0.678598,0.678598,0.281085;2.59356rad)
  ResizeMode = 0
  Support = -> [Pad019]
  Width = 107.043
FEATURE [Sketcher::SketchObject] Sketch042  label="SketchKappeGross001"
  ExternalGeometry = -> [Sketch041]
  FullyConstrained = true
  MapMode = 5
  Placement = pos=(66,-55.6624,93.0771) rot=(0.678598,-0.678598,-0.281085;3.68962rad)
  Support = -> [DatumPlane032]
  expr: Constraints[1] = <<s>>.button_kappe_durchmesser_gross
  sketch-geometry (1):
    g0: Circle CenterX=55.7063 CenterY=9.6 CenterZ=0 NormalX=0 NormalY=0 NormalZ=1 AngleXU=0 Radius=7
  constraints (2):
    c: Coincident(g0,g-3)
    c: Diameter(g0) = 14
FEATURE [PartDesign::Pad] Pad020  label="PadKappeGrossLippe001"
  BaseFeature = -> Pad019
  Direction = (-1.3e-15,0.707107,-0.707107)
  Length = 4.5
  Length2 = 10
  Placement = pos=(66,-58.4908,95.9055) rot=(0.357407,0.357407,-0.862856;1.71777rad)
  Profile = -> Sketch042
  ReferenceAxis = -> Sketch042 [N_Axis]
  Type = 0
  expr: Length = <<s>>.button_kappe_gross_hoehe
FEATURE [PartDesign::Plane] DatumPlane033
  Length = 86.754
  MapMode = 5
  Placement = pos=(66,-52.4804,89.8951) rot=(-0.678598,0.678598,0.281085;2.59356rad)
  ResizeMode = 0
  Support = -> [Pad020]
  Width = 107.043
FEATURE [Sketcher::SketchObject] Sketch043
  FullyConstrained = true
  MapMode = 5
  Placement = pos=(66,-52.4804,89.8951) rot=(-0.678598,0.678598,0.281085;2.59356rad)
  Support = -> [Pad020]
FEATURE [Sketcher::SketchObject] Sketch044  label="SketchBase001"
  ExternalGeometry = -> [Pad020]
  FullyConstrained = true
  MapMode = 5
  Placement = pos=(66,-52.4804,89.8951) rot=(-0.678598,0.678598,0.281085;2.59356rad)
  Support = -> [DatumPlane033]
  expr: Constraints[11] = <<s>>.button_base_seitenlaenge
  sketch-geometry (5):
    g0: LineSegment StartX=49.2063 StartY=3.1 StartZ=0 EndX=49.2063 EndY=16.1 EndZ=0
    g1: LineSegment StartX=49.2063 StartY=16.1 StartZ=0 EndX=62.2063 EndY=16.1 EndZ=0
    g2: LineSegment StartX=62.2063 StartY=16.1 StartZ=0 EndX=62.2063 EndY=3.1 EndZ=0
    g3: LineSegment StartX=62.2063 StartY=3.1 StartZ=0 EndX=49.2063 EndY=3.1 EndZ=0
    g4: GeomPoint X=55.7063 Y=9.6 Z=0
  constraints (12):
    c: Coincident(g0,g1)
    c: Coincident(g1,g2)
    c: Coincident(g2,g3)
    c: Coincident(g3,g0)
    c: Horizontal(g1)
    c: Horizontal(g3)
    c: Vertical(g0)
    c: Vertical(g2)
    c: Symmetric(g1,g0,g4)
    c: Coincident(g4,g-3)
    c: Equal(g2,g3)
    c: DistanceX(g3,g3) = 13
FEATURE [PartDesign::Pad] Pad021  label="PadButtonWithBase001"
  BaseFeature = -> Pad020
  Direction = (-1e-15,0.707107,-0.707107)
  Length = 15
  Length2 = 10
  Placement = pos=(66,-58.4908,95.9055) rot=(0.357407,0.357407,-0.862856;1.71777rad)
  Profile = -> Sketch044
  ReferenceAxis = -> Sketch044 [N_Axis]
  Type = 0
  expr: Length = <<s>>.button_base_extrusion
FEATURE [PartDesign::Body] Body010  label="Button002"
  Group = -> [ShapeBinder013,DatumPlane031,Sketch041,Pad019,DatumPlane032,Sketch042,Pad020,Sketch043,DatumPlane033,Sketch044,Pad021]
  Origin = -> Origin010
  Tip = -> Pad021
FEATURE [Mesh::Feature] Mesh006  label="muehle (Meshed)"
FEATURE [PartDesign::Plane] DatumPlane034
  Length = 61.1727
  MapMode = 5
  Placement = pos=(27,7.51e-14,37.4148) rot=(-0.57735,-0.57735,0.57735;2.0944rad)
  ResizeMode = 0
  Support = -> [Pocket017]
  Width = 73.5875
FEATURE [Sketcher::SketchObject] Sketch045
  ExternalGeometry = -> [Sketch027]
  FullyConstrained = true
  MapMode = 5
  Placement = pos=(27,7.51e-14,37.4148) rot=(-0.57735,-0.57735,0.57735;2.0944rad)
  Support = -> [DatumPlane034]
  sketch-geometry (4):
    g0: LineSegment StartX=-104.781 StartY=-4.7868 StartZ=0 EndX=-83.5674 EndY=-26 EndZ=0
    g1: LineSegment StartX=-93.2806 StartY=-4.7868 StartZ=0 EndX=-83.5674 EndY=-14.5 EndZ=0
    g2: LineSegment StartX=-93.2806 StartY=-4.7868 StartZ=0 EndX=-83.5674 EndY=-4.7868 EndZ=0
    g3: LineSegment StartX=-83.5674 StartY=-14.5 StartZ=0 EndX=-83.5674 EndY=-4.7868 EndZ=0
  constraints (10):
    c: Coincident(g0,g-3)
    c: Coincident(g0,g-4)
    c: PointOnObject(g1,g-3)
    c: PointOnObject(g1,g-4)
    c: Parallel(g1,g0)
    c: DistanceY(g0,g1) = 11.5
    c: Coincident(g2,g1)
    c: Coincident(g2,g-4)
    c: Coincident(g3,g1)
    c: Coincident(g3,g2)
FEATURE [PartDesign::Pocket] Pocket018  label="PocketWithCutOnButtons"
  BaseFeature = -> Pocket017
  Direction = (1,-1.1e-15,-3.6e-15)
  Length = 0
  Length2 = 5
  Placement = pos=(66,1.5e-14,37.4148) rot=(0.57735,0.57735,0.57735;2.0944rad)
  Profile = -> Sketch045
  ReferenceAxis = -> Sketch045 [N_Axis]
  Type = 3
  UpToFace = -> Pocket017 [Face6]
FEATURE [PartDesign::Body] Body007  label="Cover"
  Group = -> [ShapeBinder,ShapeBinder009,ShapeBinder010,DatumPlane020,Sketch027,Pad009,Sketch028,Pad010,DatumPlane021,Sketch029,Pad011,DatumPlane030,Pocket016,DatumPlane022,Sketch030,Pocket014,DatumPlane023,Sketch031,Pad012,Sketch032,Pad013,DatumPlane024,Sketch033,Pocket015,Sketch040,Pocket017,DatumPlane034,Sketch045,Pocket018]
  Origin = -> Origin007
  Tip = -> Pocket018
FEATURE [Part::Cut] Cut
  Base = -> Body007
  Tool = -> Body009
FEATURE [Part::Cut] Cut001
  Base = -> Cut
  Tool = -> Body008
FEATURE [Part::Cut] Cut002
  Base = -> Cut001
  Tool = -> Body010
FEATURE [Mesh::Feature] Mesh007  label="Cut002 (Meshed)"
FEATURE [Mesh::Feature] Difference
FEATURE [Mesh::Feature] Difference001  label="DifferenceMuehle"
